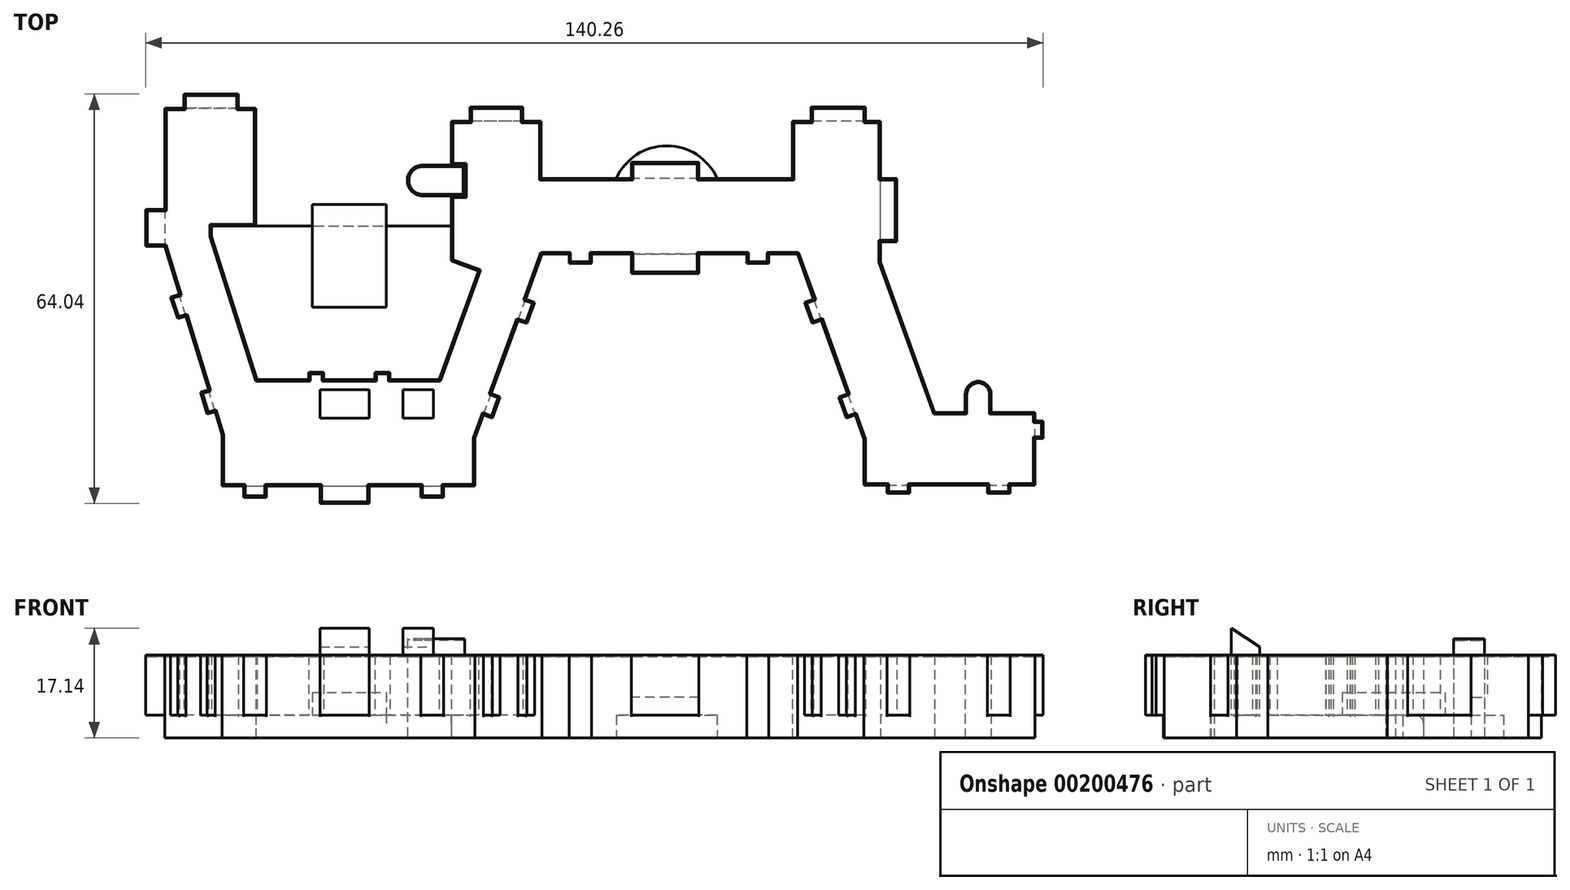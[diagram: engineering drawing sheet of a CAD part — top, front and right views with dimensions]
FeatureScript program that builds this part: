
annotation { "Feature Type Name" : "Feature", "Feature Type Description" : "" }
export const myFeature = defineFeature(function(context is Context, id is Id, definition is map)
    precondition{}
    {
        {
            var Q0;
            Q0=qCreatedBy(makeId("Top.planeOp"),FACE);
            var sketch = newSketch(context, id + "F0", { "sketchPlane" : qUnion([Q0])});
            skLineSegment(sketch, "E0", {"start": v(11.22, -2.24) * mm, "end": v(8.5, -2.24) * mm});
            skLineSegment(sketch, "E1", {"start": v(8.5, -2.24) * mm, "end": v(8.5, 0) * mm});
            skLineSegment(sketch, "E2", {"start": v(8.5, 0) * mm, "end": v(0, 0) * mm});
            skLineSegment(sketch, "E3", {"start": v(0, 0) * mm, "end": v(0, -2.24) * mm});
            skLineSegment(sketch, "E4", {"start": v(0, -2.24) * mm, "end": v(-3.01, -2.24) * mm});
            skLineSegment(sketch, "E5", {"start": v(-3.01, -2.24) * mm, "end": v(-3.01, -18.02) * mm});
            skLineSegment(sketch, "E6", {"start": v(-3.01, -18.02) * mm, "end": v(-6, -18.02) * mm});
            skLineSegment(sketch, "E7", {"start": v(-6, -18.02) * mm, "end": v(-6, -23.84) * mm});
            skLineSegment(sketch, "E8", {"start": v(-6, -23.84) * mm, "end": v(-3.01, -23.84) * mm});
            skLineSegment(sketch, "E9", {"start": v(-3.01, -23.84) * mm, "end": v(-0.72, -31.34) * mm});
            skLineSegment(sketch, "E10", {"start": v(-0.72, -31.34) * mm, "end": v(-2.13, -31.77) * mm});
            skLineSegment(sketch, "E11", {"start": v(-2.13, -31.77) * mm, "end": v(-0.97, -35.12) * mm});
            skLineSegment(sketch, "E12", {"start": v(-0.97, -35.12) * mm, "end": v(0.32, -34.73) * mm});
            skLineSegment(sketch, "E13", {"start": v(0.32, -34.73) * mm, "end": v(3.84, -46.26) * mm});
            skLineSegment(sketch, "E14", {"start": v(3.84, -46.26) * mm, "end": v(2.58, -46.65) * mm});
            skLineSegment(sketch, "E15", {"start": v(2.58, -46.65) * mm, "end": v(3.62, -50.04) * mm});
            skLineSegment(sketch, "E16", {"start": v(3.62, -50.04) * mm, "end": v(4.88, -49.65) * mm});
            skLineSegment(sketch, "E17", {"start": v(4.88, -49.65) * mm, "end": v(6, -53.3) * mm});
            skLineSegment(sketch, "E18", {"start": v(6, -53.3) * mm, "end": v(6, -61.28) * mm});
            skLineSegment(sketch, "E19", {"start": v(6, -61.28) * mm, "end": v(9.31, -61.28) * mm});
            skLineSegment(sketch, "E20", {"start": v(9.31, -61.28) * mm, "end": v(9.31, -63.05) * mm});
            skLineSegment(sketch, "E21", {"start": v(9.31, -63.05) * mm, "end": v(12.86, -63.05) * mm});
            skLineSegment(sketch, "E22", {"start": v(12.86, -63.05) * mm, "end": v(12.86, -61.28) * mm});
            skLineSegment(sketch, "E23", {"start": v(12.86, -61.28) * mm, "end": v(21.27, -61.28) * mm});
            skLineSegment(sketch, "E24", {"start": v(21.27, -61.28) * mm, "end": v(21.27, -64.04) * mm});
            skLineSegment(sketch, "E25", {"start": v(21.27, -64.04) * mm, "end": v(28.97, -64.04) * mm});
            skLineSegment(sketch, "E26", {"start": v(28.97, -64.04) * mm, "end": v(28.97, -61.28) * mm});
            skLineSegment(sketch, "E27", {"start": v(28.97, -61.28) * mm, "end": v(37, -61.28) * mm});
            skLineSegment(sketch, "E28", {"start": v(37, -61.28) * mm, "end": v(37, -63.05) * mm});
            skLineSegment(sketch, "E29", {"start": v(37, -63.05) * mm, "end": v(40.54, -63.05) * mm});
            skLineSegment(sketch, "E30", {"start": v(40.54, -63.05) * mm, "end": v(40.54, -61.28) * mm});
            skLineSegment(sketch, "E31", {"start": v(40.54, -61.28) * mm, "end": v(45.48, -61.28) * mm});
            skLineSegment(sketch, "E32", {"start": v(45.48, -61.28) * mm, "end": v(45.48, -53.82) * mm});
            skLineSegment(sketch, "E33", {"start": v(45.48, -53.82) * mm, "end": v(46.82, -50.15) * mm});
            skLineSegment(sketch, "E34", {"start": v(46.82, -50.15) * mm, "end": v(48.2, -50.7) * mm});
            skLineSegment(sketch, "E35", {"start": v(48.2, -50.7) * mm, "end": v(49.42, -47.37) * mm});
            skLineSegment(sketch, "E36", {"start": v(49.42, -47.37) * mm, "end": v(48.03, -46.82) * mm});
            skLineSegment(sketch, "E37", {"start": v(48.03, -46.82) * mm, "end": v(52.17, -35.43) * mm});
            skLineSegment(sketch, "E38", {"start": v(52.17, -35.43) * mm, "end": v(53.6, -35.9) * mm});
            skLineSegment(sketch, "E39", {"start": v(53.6, -35.9) * mm, "end": v(54.8, -32.57) * mm});
            skLineSegment(sketch, "E40", {"start": v(54.8, -32.57) * mm, "end": v(53.38, -32.1) * mm});
            skLineSegment(sketch, "E41", {"start": v(53.38, -32.1) * mm, "end": v(55.96, -25.02) * mm});
            skLineSegment(sketch, "E42", {"start": v(55.96, -25.02) * mm, "end": v(60.16, -25.02) * mm});
            skLineSegment(sketch, "E43", {"start": v(60.16, -25.02) * mm, "end": v(60.16, -26.52) * mm});
            skLineSegment(sketch, "E44", {"start": v(60.16, -26.52) * mm, "end": v(63.7, -26.52) * mm});
            skLineSegment(sketch, "E45", {"start": v(63.7, -26.52) * mm, "end": v(63.7, -25.02) * mm});
            skLineSegment(sketch, "E46", {"start": v(63.7, -25.02) * mm, "end": v(69.91, -25.02) * mm});
            skLineSegment(sketch, "E47", {"start": v(69.91, -25.02) * mm, "end": v(69.91, -28.1) * mm});
            skLineSegment(sketch, "E48", {"start": v(69.91, -28.1) * mm, "end": v(80.46, -28.1) * mm});
            skLineSegment(sketch, "E49", {"start": v(80.46, -28.1) * mm, "end": v(80.46, -25.02) * mm});
            skLineSegment(sketch, "E50", {"start": v(80.46, -25.02) * mm, "end": v(87.96, -25.02) * mm});
            skLineSegment(sketch, "E51", {"start": v(87.96, -25.02) * mm, "end": v(87.96, -26.52) * mm});
            skLineSegment(sketch, "E52", {"start": v(87.96, -26.52) * mm, "end": v(91.4, -26.52) * mm});
            skLineSegment(sketch, "E53", {"start": v(91.4, -26.52) * mm, "end": v(91.4, -25.02) * mm});
            skLineSegment(sketch, "E54", {"start": v(91.4, -25.02) * mm, "end": v(95.85, -25.02) * mm});
            skLineSegment(sketch, "E55", {"start": v(95.85, -25.02) * mm, "end": v(98.38, -32.06) * mm});
            skLineSegment(sketch, "E56", {"start": v(98.38, -32.06) * mm, "end": v(96.97, -32.57) * mm});
            skLineSegment(sketch, "E57", {"start": v(96.97, -32.57) * mm, "end": v(98.17, -35.9) * mm});
            skLineSegment(sketch, "E58", {"start": v(98.17, -35.9) * mm, "end": v(99.58, -35.4) * mm});
            skLineSegment(sketch, "E59", {"start": v(99.58, -35.4) * mm, "end": v(103.7, -46.87) * mm});
            skLineSegment(sketch, "E60", {"start": v(103.7, -46.87) * mm, "end": v(102.29, -47.37) * mm});
            skLineSegment(sketch, "E61", {"start": v(102.29, -47.37) * mm, "end": v(103.49, -50.7) * mm});
            skLineSegment(sketch, "E62", {"start": v(103.49, -50.7) * mm, "end": v(104.9, -50.2) * mm});
            skLineSegment(sketch, "E63", {"start": v(104.9, -50.2) * mm, "end": v(106.25, -53.96) * mm});
            skLineSegment(sketch, "E64", {"start": v(106.25, -53.96) * mm, "end": v(106.25, -61.16) * mm});
            skLineSegment(sketch, "E65", {"start": v(106.25, -61.16) * mm, "end": v(109.85, -61.16) * mm});
            skLineSegment(sketch, "E66", {"start": v(109.85, -61.16) * mm, "end": v(109.85, -62.43) * mm});
            skLineSegment(sketch, "E67", {"start": v(109.85, -62.43) * mm, "end": v(113.4, -62.43) * mm});
            skLineSegment(sketch, "E68", {"start": v(113.4, -62.43) * mm, "end": v(113.4, -61.16) * mm});
            skLineSegment(sketch, "E69", {"start": v(113.4, -61.16) * mm, "end": v(125.52, -61.16) * mm});
            skLineSegment(sketch, "E70", {"start": v(125.52, -61.16) * mm, "end": v(125.52, -62.43) * mm});
            skLineSegment(sketch, "E71", {"start": v(125.52, -62.43) * mm, "end": v(129.06, -62.43) * mm});
            skLineSegment(sketch, "E72", {"start": v(129.06, -62.43) * mm, "end": v(129.06, -61.16) * mm});
            skLineSegment(sketch, "E73", {"start": v(129.06, -61.16) * mm, "end": v(133, -61.16) * mm});
            skLineSegment(sketch, "E74", {"start": v(133, -61.16) * mm, "end": v(133, -53.89) * mm});
            skLineSegment(sketch, "E75", {"start": v(133, -53.89) * mm, "end": v(134.26, -53.89) * mm});
            skLineSegment(sketch, "E76", {"start": v(134.26, -53.89) * mm, "end": v(134.26, -51.15) * mm});
            skLineSegment(sketch, "E77", {"start": v(134.26, -51.15) * mm, "end": v(133, -51.15) * mm});
            skLineSegment(sketch, "E78", {"start": v(133, -51.15) * mm, "end": v(133, -49.82) * mm});
            skLineSegment(sketch, "E79", {"start": v(133, -49.82) * mm, "end": v(126.13, -49.82) * mm});
            skLineSegment(sketch, "E80", {"start": v(126.13, -49.82) * mm, "end": v(126.13, -46.96) * mm});
            skLineSegment(sketch, "E81", {"start": v(122.07, -46.96) * mm, "end": v(122.07, -49.82) * mm});
            skLineSegment(sketch, "E82", {"start": v(122.07, -49.82) * mm, "end": v(117.3, -49.82) * mm});
            skLineSegment(sketch, "E83", {"start": v(117.3, -49.82) * mm, "end": v(108.85, -26.28) * mm});
            skLineSegment(sketch, "E84", {"start": v(108.85, -26.28) * mm, "end": v(108.85, -23.13) * mm});
            skLineSegment(sketch, "E85", {"start": v(108.85, -23.13) * mm, "end": v(111.35, -23.13) * mm});
            skLineSegment(sketch, "E86", {"start": v(111.35, -23.13) * mm, "end": v(111.35, -13.22) * mm});
            skLineSegment(sketch, "E87", {"start": v(111.35, -13.22) * mm, "end": v(108.85, -13.22) * mm});
            skLineSegment(sketch, "E88", {"start": v(108.85, -13.22) * mm, "end": v(108.85, -4.25) * mm});
            skLineSegment(sketch, "E89", {"start": v(108.85, -4.25) * mm, "end": v(106.47, -4.25) * mm});
            skLineSegment(sketch, "E90", {"start": v(106.47, -4.25) * mm, "end": v(106.47, -2.03) * mm});
            skLineSegment(sketch, "E91", {"start": v(106.47, -2.03) * mm, "end": v(98, -2.03) * mm});
            skLineSegment(sketch, "E92", {"start": v(98, -2.03) * mm, "end": v(98, -4.25) * mm});
            skLineSegment(sketch, "E93", {"start": v(98, -4.25) * mm, "end": v(95.07, -4.25) * mm});
            skLineSegment(sketch, "E94", {"start": v(95.07, -4.25) * mm, "end": v(95.07, -13.22) * mm});
            skLineSegment(sketch, "E95", {"start": v(95.07, -13.22) * mm, "end": v(80.46, -13.22) * mm});
            skLineSegment(sketch, "E96", {"start": v(80.46, -13.22) * mm, "end": v(80.46, -10.66) * mm});
            skLineSegment(sketch, "E97", {"start": v(80.46, -10.66) * mm, "end": v(69.91, -10.66) * mm});
            skLineSegment(sketch, "E98", {"start": v(69.91, -10.66) * mm, "end": v(69.91, -13.22) * mm});
            skLineSegment(sketch, "E99", {"start": v(69.91, -13.22) * mm, "end": v(55.8, -13.22) * mm});
            skLineSegment(sketch, "E100", {"start": v(55.8, -13.22) * mm, "end": v(55.8, -4.25) * mm});
            skLineSegment(sketch, "E101", {"start": v(55.8, -4.25) * mm, "end": v(52.93, -4.25) * mm});
            skLineSegment(sketch, "E102", {"start": v(52.93, -4.25) * mm, "end": v(52.93, -2.03) * mm});
            skLineSegment(sketch, "E103", {"start": v(52.93, -2.03) * mm, "end": v(44.68, -2.03) * mm});
            skLineSegment(sketch, "E104", {"start": v(44.68, -2.03) * mm, "end": v(44.68, -4.25) * mm});
            skLineSegment(sketch, "E105", {"start": v(44.68, -4.25) * mm, "end": v(41.8, -4.25) * mm});
            skLineSegment(sketch, "E106", {"start": v(41.8, -4.25) * mm, "end": v(41.8, -11.12) * mm});
            skLineSegment(sketch, "E107", {"start": v(41.8, -11.12) * mm, "end": v(37.3, -11.12) * mm});
            skLineSegment(sketch, "E108", {"start": v(37.3, -15.94) * mm, "end": v(41.79, -15.94) * mm});
            skLineSegment(sketch, "E109", {"start": v(41.79, -15.94) * mm, "end": v(41.79, -26.13) * mm});
            skLineSegment(sketch, "E110", {"start": v(41.79, -26.13) * mm, "end": v(46.05, -27.68) * mm});
            skLineSegment(sketch, "E111", {"start": v(46.05, -27.68) * mm, "end": v(39.88, -44.65) * mm});
            skLineSegment(sketch, "E112", {"start": v(39.88, -44.65) * mm, "end": v(32.18, -44.65) * mm});
            skLineSegment(sketch, "E113", {"start": v(32.18, -44.65) * mm, "end": v(32.18, -43.48) * mm});
            skLineSegment(sketch, "E114", {"start": v(32.18, -43.48) * mm, "end": v(29.86, -43.48) * mm});
            skLineSegment(sketch, "E115", {"start": v(29.86, -43.48) * mm, "end": v(29.86, -44.65) * mm});
            skLineSegment(sketch, "E116", {"start": v(29.86, -44.65) * mm, "end": v(21.83, -44.65) * mm});
            skLineSegment(sketch, "E117", {"start": v(21.83, -44.65) * mm, "end": v(21.83, -43.48) * mm});
            skLineSegment(sketch, "E118", {"start": v(21.83, -43.48) * mm, "end": v(19.5, -43.48) * mm});
            skLineSegment(sketch, "E119", {"start": v(19.5, -43.48) * mm, "end": v(19.5, -44.65) * mm});
            skLineSegment(sketch, "E120", {"start": v(19.5, -44.65) * mm, "end": v(11.42, -44.65) * mm});
            skLineSegment(sketch, "E121", {"start": v(11.42, -44.65) * mm, "end": v(4.3, -22.29) * mm});
            skLineSegment(sketch, "E122", {"start": v(4.3, -22.29) * mm, "end": v(4.3, -20.63) * mm});
            skLineSegment(sketch, "E123", {"start": v(4.3, -20.63) * mm, "end": v(11.22, -20.63) * mm});
            skLineSegment(sketch, "E124", {"start": v(11.22, -20.63) * mm, "end": v(11.22, -2.24) * mm});
            skArc(sketch, "E125", {"start": v(37.3, -11.12) * mm, "mid": v(34.9, -13.53) * mm, "end": v(37.3, -15.94) * mm});
            skArc(sketch, "E126", {"start": v(126.13, -46.96) * mm, "mid": v(124.1, -44.93) * mm, "end": v(122.07, -46.96) * mm});
            skLineSegment(sketch, "E127", {"start": v(41.8, -11.12) * mm, "end": v(43.9, -11.12) * mm});
            skLineSegment(sketch, "E128", {"start": v(43.9, -11.12) * mm, "end": v(43.9, -15.94) * mm});
            skLineSegment(sketch, "E129", {"start": v(43.9, -15.94) * mm, "end": v(41.79, -15.94) * mm});
            skLineSegment(sketch, "E130", {"start": v(-3.01, -18.02) * mm, "end": v(-3.01, -23.84) * mm, "construction": true});
            skSolve(sketch);
        }
        {
            var Q0;
            Q0 = qSketchRegion(id + "F0", true);
            extrude(context, id + "F1", {"entities" : qUnion([Q0]), "depth" : 12.7 * mm});
        }
        {
            var Q0;
            Q0=makeQuery(id+"F0.imprint","IMPRINT",FACE,{"disambiguationData":[TD([[makeQuery(id+"F0.imprint","IMPRINT",EDGE,{"derivedFrom":sQuery(id+"F0.wireOp",EDGE,"E107")}),1.0]])]});
            extrude(context, id + "F2", {"entities" : qUnion([Q0]), "operationType" : NewBodyOperationType.ADD, "depth" : 15.24 * mm});
        }
        {
            var Q0;
            Q0=makeQuery(id+"F1.opExtrude","CAP_FACE",FACE,{"disambiguationData":[OSD([sQuery(id+"F0.wireOp",EDGE,"E0"),sQuery(id+"F0.wireOp",EDGE,"E1"),sQuery(id+"F0.wireOp",EDGE,"E2"),sQuery(id+"F0.wireOp",EDGE,"E3"),sQuery(id+"F0.wireOp",EDGE,"E4"),sQuery(id+"F0.wireOp",EDGE,"E5"),sQuery(id+"F0.wireOp",EDGE,"E6"),sQuery(id+"F0.wireOp",EDGE,"E7"),sQuery(id+"F0.wireOp",EDGE,"E8"),sQuery(id+"F0.wireOp",EDGE,"E9"),sQuery(id+"F0.wireOp",EDGE,"E10"),sQuery(id+"F0.wireOp",EDGE,"E11"),sQuery(id+"F0.wireOp",EDGE,"E12"),sQuery(id+"F0.wireOp",EDGE,"E13"),sQuery(id+"F0.wireOp",EDGE,"E14"),sQuery(id+"F0.wireOp",EDGE,"E15"),sQuery(id+"F0.wireOp",EDGE,"E16"),sQuery(id+"F0.wireOp",EDGE,"E17"),sQuery(id+"F0.wireOp",EDGE,"E18"),sQuery(id+"F0.wireOp",EDGE,"E19"),sQuery(id+"F0.wireOp",EDGE,"E20"),sQuery(id+"F0.wireOp",EDGE,"E21"),sQuery(id+"F0.wireOp",EDGE,"E22"),sQuery(id+"F0.wireOp",EDGE,"E23"),sQuery(id+"F0.wireOp",EDGE,"E24"),sQuery(id+"F0.wireOp",EDGE,"E25"),sQuery(id+"F0.wireOp",EDGE,"E26"),sQuery(id+"F0.wireOp",EDGE,"E27"),sQuery(id+"F0.wireOp",EDGE,"E28"),sQuery(id+"F0.wireOp",EDGE,"E29"),sQuery(id+"F0.wireOp",EDGE,"E30"),sQuery(id+"F0.wireOp",EDGE,"E31"),sQuery(id+"F0.wireOp",EDGE,"E32"),sQuery(id+"F0.wireOp",EDGE,"E33"),sQuery(id+"F0.wireOp",EDGE,"E34"),sQuery(id+"F0.wireOp",EDGE,"E35"),sQuery(id+"F0.wireOp",EDGE,"E36"),sQuery(id+"F0.wireOp",EDGE,"E37"),sQuery(id+"F0.wireOp",EDGE,"E38"),sQuery(id+"F0.wireOp",EDGE,"E39"),sQuery(id+"F0.wireOp",EDGE,"E40"),sQuery(id+"F0.wireOp",EDGE,"E41"),sQuery(id+"F0.wireOp",EDGE,"E42"),sQuery(id+"F0.wireOp",EDGE,"E43"),sQuery(id+"F0.wireOp",EDGE,"E44"),sQuery(id+"F0.wireOp",EDGE,"E45"),sQuery(id+"F0.wireOp",EDGE,"E46"),sQuery(id+"F0.wireOp",EDGE,"E47"),sQuery(id+"F0.wireOp",EDGE,"E48"),sQuery(id+"F0.wireOp",EDGE,"E49"),sQuery(id+"F0.wireOp",EDGE,"E50"),sQuery(id+"F0.wireOp",EDGE,"E51"),sQuery(id+"F0.wireOp",EDGE,"E52"),sQuery(id+"F0.wireOp",EDGE,"E53"),sQuery(id+"F0.wireOp",EDGE,"E54"),sQuery(id+"F0.wireOp",EDGE,"E55"),sQuery(id+"F0.wireOp",EDGE,"E56"),sQuery(id+"F0.wireOp",EDGE,"E57"),sQuery(id+"F0.wireOp",EDGE,"E58"),sQuery(id+"F0.wireOp",EDGE,"E59"),sQuery(id+"F0.wireOp",EDGE,"E60"),sQuery(id+"F0.wireOp",EDGE,"E61"),sQuery(id+"F0.wireOp",EDGE,"E62"),sQuery(id+"F0.wireOp",EDGE,"E63"),sQuery(id+"F0.wireOp",EDGE,"E64"),sQuery(id+"F0.wireOp",EDGE,"E65"),sQuery(id+"F0.wireOp",EDGE,"E66"),sQuery(id+"F0.wireOp",EDGE,"E67"),sQuery(id+"F0.wireOp",EDGE,"E68"),sQuery(id+"F0.wireOp",EDGE,"E69"),sQuery(id+"F0.wireOp",EDGE,"E70"),sQuery(id+"F0.wireOp",EDGE,"E71"),sQuery(id+"F0.wireOp",EDGE,"E72"),sQuery(id+"F0.wireOp",EDGE,"E73"),sQuery(id+"F0.wireOp",EDGE,"E74"),sQuery(id+"F0.wireOp",EDGE,"E75"),sQuery(id+"F0.wireOp",EDGE,"E76"),sQuery(id+"F0.wireOp",EDGE,"E77"),sQuery(id+"F0.wireOp",EDGE,"E78"),sQuery(id+"F0.wireOp",EDGE,"E79"),sQuery(id+"F0.wireOp",EDGE,"E80"),sQuery(id+"F0.wireOp",EDGE,"E81"),sQuery(id+"F0.wireOp",EDGE,"E82"),sQuery(id+"F0.wireOp",EDGE,"E83"),sQuery(id+"F0.wireOp",EDGE,"E84"),sQuery(id+"F0.wireOp",EDGE,"E85"),sQuery(id+"F0.wireOp",EDGE,"E86"),sQuery(id+"F0.wireOp",EDGE,"E87"),sQuery(id+"F0.wireOp",EDGE,"E88"),sQuery(id+"F0.wireOp",EDGE,"E89"),sQuery(id+"F0.wireOp",EDGE,"E90"),sQuery(id+"F0.wireOp",EDGE,"E91"),sQuery(id+"F0.wireOp",EDGE,"E92"),sQuery(id+"F0.wireOp",EDGE,"E93"),sQuery(id+"F0.wireOp",EDGE,"E94"),sQuery(id+"F0.wireOp",EDGE,"E95"),sQuery(id+"F0.wireOp",EDGE,"E96"),sQuery(id+"F0.wireOp",EDGE,"E97"),sQuery(id+"F0.wireOp",EDGE,"E98"),sQuery(id+"F0.wireOp",EDGE,"E99"),sQuery(id+"F0.wireOp",EDGE,"E100"),sQuery(id+"F0.wireOp",EDGE,"E101"),sQuery(id+"F0.wireOp",EDGE,"E102"),sQuery(id+"F0.wireOp",EDGE,"E103"),sQuery(id+"F0.wireOp",EDGE,"E104"),sQuery(id+"F0.wireOp",EDGE,"E105"),sQuery(id+"F0.wireOp",EDGE,"E106"),sQuery(id+"F0.wireOp",EDGE,"E107"),sQuery(id+"F0.wireOp",EDGE,"E108"),sQuery(id+"F0.wireOp",EDGE,"E109"),sQuery(id+"F0.wireOp",EDGE,"E110"),sQuery(id+"F0.wireOp",EDGE,"E111"),sQuery(id+"F0.wireOp",EDGE,"E112"),sQuery(id+"F0.wireOp",EDGE,"E113"),sQuery(id+"F0.wireOp",EDGE,"E114"),sQuery(id+"F0.wireOp",EDGE,"E115"),sQuery(id+"F0.wireOp",EDGE,"E116"),sQuery(id+"F0.wireOp",EDGE,"E117"),sQuery(id+"F0.wireOp",EDGE,"E118"),sQuery(id+"F0.wireOp",EDGE,"E119"),sQuery(id+"F0.wireOp",EDGE,"E120"),sQuery(id+"F0.wireOp",EDGE,"E121"),sQuery(id+"F0.wireOp",EDGE,"E122"),sQuery(id+"F0.wireOp",EDGE,"E123"),sQuery(id+"F0.wireOp",EDGE,"E124"),sQuery(id+"F0.wireOp",EDGE,"E125"),sQuery(id+"F0.wireOp",EDGE,"E126")])],"isStart":false});
            var sketch = newSketch(context, id + "F3", { "sketchPlane" : qUnion([Q0])});
            skLineSegment(sketch, "E131.0", {"start": v(42.05, -4.5) * mm, "end": v(42.05, -10.87) * mm});
            skLineSegment(sketch, "E131.1", {"start": v(44.93, -4.5) * mm, "end": v(42.05, -4.5) * mm});
            skLineSegment(sketch, "E131.2", {"start": v(44.93, -2.28) * mm, "end": v(44.93, -4.5) * mm});
            skLineSegment(sketch, "E131.3", {"start": v(52.68, -2.28) * mm, "end": v(44.93, -2.28) * mm});
            skLineSegment(sketch, "E131.4", {"start": v(52.68, -4.5) * mm, "end": v(52.68, -2.28) * mm});
            skLineSegment(sketch, "E131.5", {"start": v(55.56, -4.5) * mm, "end": v(52.68, -4.5) * mm});
            skLineSegment(sketch, "E131.6", {"start": v(55.56, -13.47) * mm, "end": v(55.56, -4.5) * mm});
            skLineSegment(sketch, "E131.7", {"start": v(70.17, -13.47) * mm, "end": v(55.56, -13.47) * mm});
            skLineSegment(sketch, "E131.8", {"start": v(70.17, -10.91) * mm, "end": v(70.17, -13.47) * mm});
            skLineSegment(sketch, "E131.9", {"start": v(80.2, -10.91) * mm, "end": v(70.17, -10.91) * mm});
            skLineSegment(sketch, "E131.10", {"start": v(80.2, -13.47) * mm, "end": v(80.2, -10.91) * mm});
            skLineSegment(sketch, "E131.11", {"start": v(95.32, -13.47) * mm, "end": v(80.2, -13.47) * mm});
            skLineSegment(sketch, "E131.12", {"start": v(95.32, -4.5) * mm, "end": v(95.32, -13.47) * mm});
            skLineSegment(sketch, "E131.13", {"start": v(98.26, -4.5) * mm, "end": v(95.32, -4.5) * mm});
            skLineSegment(sketch, "E131.14", {"start": v(98.26, -2.28) * mm, "end": v(98.26, -4.5) * mm});
            skLineSegment(sketch, "E131.15", {"start": v(106.22, -2.28) * mm, "end": v(98.26, -2.28) * mm});
            skLineSegment(sketch, "E131.16", {"start": v(106.22, -4.5) * mm, "end": v(106.22, -2.28) * mm});
            skLineSegment(sketch, "E131.17", {"start": v(108.6, -4.5) * mm, "end": v(106.22, -4.5) * mm});
            skLineSegment(sketch, "E131.18", {"start": v(108.6, -13.47) * mm, "end": v(108.6, -4.5) * mm});
            skLineSegment(sketch, "E131.19", {"start": v(111.1, -13.47) * mm, "end": v(108.6, -13.47) * mm});
            skLineSegment(sketch, "E131.20", {"start": v(111.1, -22.87) * mm, "end": v(111.1, -13.47) * mm});
            skLineSegment(sketch, "E131.21", {"start": v(108.6, -22.87) * mm, "end": v(111.1, -22.87) * mm});
            skLineSegment(sketch, "E131.22", {"start": v(108.6, -26.33) * mm, "end": v(108.6, -22.87) * mm});
            skLineSegment(sketch, "E131.23", {"start": v(117.13, -50.07) * mm, "end": v(108.6, -26.33) * mm});
            skLineSegment(sketch, "E131.24", {"start": v(122.32, -50.07) * mm, "end": v(117.13, -50.07) * mm});
            skLineSegment(sketch, "E131.25", {"start": v(122.32, -46.96) * mm, "end": v(122.32, -50.07) * mm});
            skArc(sketch, "E131.26", {"start": v(125.87, -46.96) * mm, "mid": v(124.1, -45.19) * mm, "end": v(122.32, -46.96) * mm});
            skLineSegment(sketch, "E131.27", {"start": v(125.87, -50.07) * mm, "end": v(125.87, -46.96) * mm});
            skLineSegment(sketch, "E131.28", {"start": v(132.74, -50.07) * mm, "end": v(125.87, -50.07) * mm});
            skLineSegment(sketch, "E131.29", {"start": v(132.74, -51.4) * mm, "end": v(132.74, -50.07) * mm});
            skLineSegment(sketch, "E131.30", {"start": v(28.72, -61.02) * mm, "end": v(37.25, -61.02) * mm});
            skLineSegment(sketch, "E131.31", {"start": v(28.72, -63.8) * mm, "end": v(28.72, -61.02) * mm});
            skLineSegment(sketch, "E131.32", {"start": v(21.53, -63.8) * mm, "end": v(28.72, -63.8) * mm});
            skLineSegment(sketch, "E131.33", {"start": v(21.53, -61.02) * mm, "end": v(21.53, -63.8) * mm});
            skLineSegment(sketch, "E131.34", {"start": v(12.6, -61.02) * mm, "end": v(21.53, -61.02) * mm});
            skLineSegment(sketch, "E131.35", {"start": v(12.6, -62.8) * mm, "end": v(12.6, -61.02) * mm});
            skLineSegment(sketch, "E131.36", {"start": v(9.57, -62.8) * mm, "end": v(12.6, -62.8) * mm});
            skLineSegment(sketch, "E131.37", {"start": v(9.57, -61.02) * mm, "end": v(9.57, -62.8) * mm});
            skLineSegment(sketch, "E131.38", {"start": v(6.25, -61.02) * mm, "end": v(9.57, -61.02) * mm});
            skLineSegment(sketch, "E131.39", {"start": v(6.25, -53.27) * mm, "end": v(6.25, -61.02) * mm});
            skLineSegment(sketch, "E131.40", {"start": v(5.04, -49.34) * mm, "end": v(6.25, -53.27) * mm});
            skLineSegment(sketch, "E131.41", {"start": v(3.79, -49.72) * mm, "end": v(5.04, -49.34) * mm});
            skLineSegment(sketch, "E131.42", {"start": v(2.9, -46.82) * mm, "end": v(3.79, -49.72) * mm});
            skLineSegment(sketch, "E131.43", {"start": v(4.16, -46.43) * mm, "end": v(2.9, -46.82) * mm});
            skLineSegment(sketch, "E131.44", {"start": v(0.48, -34.4) * mm, "end": v(4.16, -46.43) * mm});
            skLineSegment(sketch, "E131.45", {"start": v(-0.81, -34.8) * mm, "end": v(0.48, -34.4) * mm});
            skLineSegment(sketch, "E131.46", {"start": v(-1.8, -31.94) * mm, "end": v(-0.81, -34.8) * mm});
            skLineSegment(sketch, "E131.47", {"start": v(-0.4, -31.5) * mm, "end": v(-1.8, -31.94) * mm});
            skLineSegment(sketch, "E131.48", {"start": v(-2.82, -23.58) * mm, "end": v(-0.4, -31.5) * mm});
            skLineSegment(sketch, "E131.49", {"start": v(-5.75, -23.58) * mm, "end": v(-2.82, -23.58) * mm});
            skLineSegment(sketch, "E131.50", {"start": v(-5.75, -18.28) * mm, "end": v(-5.75, -23.58) * mm});
            skLineSegment(sketch, "E131.51", {"start": v(-2.76, -18.28) * mm, "end": v(-5.75, -18.28) * mm});
            skLineSegment(sketch, "E131.52", {"start": v(-2.76, -2.5) * mm, "end": v(-2.76, -18.28) * mm});
            skLineSegment(sketch, "E131.53", {"start": v(0.25, -2.5) * mm, "end": v(-2.76, -2.5) * mm});
            skLineSegment(sketch, "E131.54", {"start": v(30.1, -44.9) * mm, "end": v(21.57, -44.9) * mm});
            skLineSegment(sketch, "E131.55", {"start": v(30.1, -43.74) * mm, "end": v(30.1, -44.9) * mm});
            skLineSegment(sketch, "E131.56", {"start": v(31.93, -43.74) * mm, "end": v(30.1, -43.74) * mm});
            skLineSegment(sketch, "E131.57", {"start": v(31.93, -44.9) * mm, "end": v(31.93, -43.74) * mm});
            skLineSegment(sketch, "E131.58", {"start": v(40.06, -44.9) * mm, "end": v(31.93, -44.9) * mm});
            skLineSegment(sketch, "E131.59", {"start": v(46.37, -27.52) * mm, "end": v(40.06, -44.9) * mm});
            skLineSegment(sketch, "E131.60", {"start": v(44.16, -10.87) * mm, "end": v(44.16, -16.2) * mm});
            skLineSegment(sketch, "E131.61", {"start": v(44.16, -16.2) * mm, "end": v(42.04, -16.2) * mm});
            skLineSegment(sketch, "E131.62", {"start": v(42.04, -16.2) * mm, "end": v(42.04, -25.95) * mm});
            skLineSegment(sketch, "E131.63", {"start": v(42.04, -25.95) * mm, "end": v(46.37, -27.52) * mm});
            skLineSegment(sketch, "E131.64", {"start": v(21.57, -44.9) * mm, "end": v(21.57, -43.74) * mm});
            skLineSegment(sketch, "E131.65", {"start": v(21.57, -43.74) * mm, "end": v(19.76, -43.74) * mm});
            skLineSegment(sketch, "E131.66", {"start": v(19.76, -43.74) * mm, "end": v(19.76, -44.9) * mm});
            skLineSegment(sketch, "E131.67", {"start": v(19.76, -44.9) * mm, "end": v(11.23, -44.9) * mm});
            skLineSegment(sketch, "E131.68", {"start": v(11.23, -44.9) * mm, "end": v(4.04, -22.33) * mm});
            skLineSegment(sketch, "E131.69", {"start": v(4.04, -22.33) * mm, "end": v(4.04, -20.37) * mm});
            skLineSegment(sketch, "E131.70", {"start": v(4.04, -20.37) * mm, "end": v(10.96, -20.37) * mm});
            skLineSegment(sketch, "E131.71", {"start": v(10.96, -20.37) * mm, "end": v(10.96, -2.5) * mm});
            skLineSegment(sketch, "E131.72", {"start": v(10.96, -2.5) * mm, "end": v(8.25, -2.5) * mm});
            skLineSegment(sketch, "E131.73", {"start": v(8.25, -2.5) * mm, "end": v(8.25, -0.25) * mm});
            skLineSegment(sketch, "E131.74", {"start": v(8.25, -0.25) * mm, "end": v(0.25, -0.25) * mm});
            skLineSegment(sketch, "E131.75", {"start": v(0.25, -0.25) * mm, "end": v(0.25, -2.5) * mm});
            skLineSegment(sketch, "E131.76", {"start": v(37.25, -61.02) * mm, "end": v(37.25, -62.8) * mm});
            skLineSegment(sketch, "E131.77", {"start": v(37.25, -62.8) * mm, "end": v(40.29, -62.8) * mm});
            skLineSegment(sketch, "E131.78", {"start": v(40.29, -62.8) * mm, "end": v(40.29, -61.02) * mm});
            skLineSegment(sketch, "E131.79", {"start": v(40.29, -61.02) * mm, "end": v(45.23, -61.02) * mm});
            skLineSegment(sketch, "E131.80", {"start": v(45.23, -61.02) * mm, "end": v(45.23, -53.78) * mm});
            skLineSegment(sketch, "E131.81", {"start": v(45.23, -53.78) * mm, "end": v(46.67, -49.82) * mm});
            skLineSegment(sketch, "E131.82", {"start": v(46.67, -49.82) * mm, "end": v(48.06, -50.37) * mm});
            skLineSegment(sketch, "E131.83", {"start": v(48.06, -50.37) * mm, "end": v(49.1, -47.52) * mm});
            skLineSegment(sketch, "E131.84", {"start": v(49.1, -47.52) * mm, "end": v(47.7, -46.97) * mm});
            skLineSegment(sketch, "E131.85", {"start": v(47.7, -46.97) * mm, "end": v(52.02, -35.1) * mm});
            skLineSegment(sketch, "E131.86", {"start": v(52.02, -35.1) * mm, "end": v(53.44, -35.58) * mm});
            skLineSegment(sketch, "E131.87", {"start": v(53.44, -35.58) * mm, "end": v(54.48, -32.73) * mm});
            skLineSegment(sketch, "E131.88", {"start": v(54.48, -32.73) * mm, "end": v(53.05, -32.26) * mm});
            skLineSegment(sketch, "E131.89", {"start": v(53.05, -32.26) * mm, "end": v(55.78, -24.77) * mm});
            skLineSegment(sketch, "E131.90", {"start": v(55.78, -24.77) * mm, "end": v(60.42, -24.77) * mm});
            skLineSegment(sketch, "E131.91", {"start": v(60.42, -24.77) * mm, "end": v(60.42, -26.27) * mm});
            skLineSegment(sketch, "E131.92", {"start": v(60.42, -26.27) * mm, "end": v(63.45, -26.27) * mm});
            skLineSegment(sketch, "E131.93", {"start": v(63.45, -26.27) * mm, "end": v(63.45, -24.77) * mm});
            skLineSegment(sketch, "E131.94", {"start": v(63.45, -24.77) * mm, "end": v(70.17, -24.77) * mm});
            skLineSegment(sketch, "E131.95", {"start": v(70.17, -24.77) * mm, "end": v(70.17, -27.85) * mm});
            skLineSegment(sketch, "E131.96", {"start": v(70.17, -27.85) * mm, "end": v(80.2, -27.85) * mm});
            skLineSegment(sketch, "E131.97", {"start": v(80.2, -27.85) * mm, "end": v(80.2, -24.77) * mm});
            skLineSegment(sketch, "E131.98", {"start": v(80.2, -24.77) * mm, "end": v(88.21, -24.77) * mm});
            skLineSegment(sketch, "E131.99", {"start": v(88.21, -24.77) * mm, "end": v(88.21, -26.27) * mm});
            skLineSegment(sketch, "E131.100", {"start": v(88.21, -26.27) * mm, "end": v(91.14, -26.27) * mm});
            skLineSegment(sketch, "E131.101", {"start": v(91.14, -26.27) * mm, "end": v(91.14, -24.77) * mm});
            skLineSegment(sketch, "E131.102", {"start": v(91.14, -24.77) * mm, "end": v(96.03, -24.77) * mm});
            skLineSegment(sketch, "E131.103", {"start": v(96.03, -24.77) * mm, "end": v(98.7, -32.22) * mm});
            skLineSegment(sketch, "E131.104", {"start": v(98.7, -32.22) * mm, "end": v(97.3, -32.72) * mm});
            skLineSegment(sketch, "E131.105", {"start": v(97.3, -32.72) * mm, "end": v(98.32, -35.58) * mm});
            skLineSegment(sketch, "E131.106", {"start": v(42.05, -10.87) * mm, "end": v(44.16, -10.87) * mm});
            skLineSegment(sketch, "E131.107", {"start": v(98.32, -35.58) * mm, "end": v(99.73, -35.07) * mm});
            skLineSegment(sketch, "E131.108", {"start": v(99.73, -35.07) * mm, "end": v(104.02, -47.02) * mm});
            skLineSegment(sketch, "E131.109", {"start": v(104.02, -47.02) * mm, "end": v(102.61, -47.53) * mm});
            skLineSegment(sketch, "E131.110", {"start": v(102.61, -47.53) * mm, "end": v(103.64, -50.38) * mm});
            skLineSegment(sketch, "E131.111", {"start": v(103.64, -50.38) * mm, "end": v(105.05, -49.88) * mm});
            skLineSegment(sketch, "E131.112", {"start": v(105.05, -49.88) * mm, "end": v(106.5, -53.92) * mm});
            skLineSegment(sketch, "E131.113", {"start": v(106.5, -53.92) * mm, "end": v(106.5, -60.9) * mm});
            skLineSegment(sketch, "E131.114", {"start": v(106.5, -60.9) * mm, "end": v(110.1, -60.9) * mm});
            skLineSegment(sketch, "E131.115", {"start": v(110.1, -60.9) * mm, "end": v(110.1, -62.18) * mm});
            skLineSegment(sketch, "E131.116", {"start": v(110.1, -62.18) * mm, "end": v(113.14, -62.18) * mm});
            skLineSegment(sketch, "E131.117", {"start": v(113.14, -62.18) * mm, "end": v(113.14, -60.9) * mm});
            skLineSegment(sketch, "E131.118", {"start": v(113.14, -60.9) * mm, "end": v(125.77, -60.9) * mm});
            skLineSegment(sketch, "E131.119", {"start": v(125.77, -60.9) * mm, "end": v(125.77, -62.18) * mm});
            skLineSegment(sketch, "E131.120", {"start": v(125.77, -62.18) * mm, "end": v(128.8, -62.18) * mm});
            skLineSegment(sketch, "E131.121", {"start": v(128.8, -62.18) * mm, "end": v(128.8, -60.9) * mm});
            skLineSegment(sketch, "E131.122", {"start": v(128.8, -60.9) * mm, "end": v(132.74, -60.9) * mm});
            skLineSegment(sketch, "E131.123", {"start": v(132.74, -60.9) * mm, "end": v(132.74, -53.63) * mm});
            skLineSegment(sketch, "E131.124", {"start": v(132.74, -53.63) * mm, "end": v(134.01, -53.63) * mm});
            skLineSegment(sketch, "E131.125", {"start": v(134.01, -53.63) * mm, "end": v(134.01, -51.4) * mm});
            skLineSegment(sketch, "E131.126", {"start": v(134.01, -51.4) * mm, "end": v(132.74, -51.4) * mm});
            skSolve(sketch);
        }
        {
            var Q0;
            Q0=makeQuery(id+"F3.imprint","IMPRINT",FACE,{"disambiguationData":[TD([[makeQuery(id+"F3.imprint","IMPRINT",EDGE,{"derivedFrom":sQuery(id+"F3.wireOp",EDGE,"E131.0")}),-1.0]])]});
            extrude(context, id + "F4", {"entities" : qUnion([Q0]), "operationType" : NewBodyOperationType.ADD, "depth" : 0.25 * mm});
        }
        {
            var Q0;
            Q0=makeQuery(id+"F2.opExtrude","CAP_FACE",FACE,{"disambiguationData":[OSD([sQuery(id+"F0.wireOp",EDGE,"E107"),sQuery(id+"F0.wireOp",EDGE,"E108"),sQuery(id+"F0.wireOp",EDGE,"E125"),sQuery(id+"F0.wireOp",EDGE,"E127"),sQuery(id+"F0.wireOp",EDGE,"E128"),sQuery(id+"F0.wireOp",EDGE,"E129")])],"isStart":false});
            var sketch = newSketch(context, id + "F5", { "sketchPlane" : qUnion([Q0])});
            skLineSegment(sketch, "E132.0", {"start": v(43.65, -11.37) * mm, "end": v(37.3, -11.37) * mm});
            skLineSegment(sketch, "E132.1", {"start": v(43.65, -15.68) * mm, "end": v(43.65, -11.37) * mm});
            skLineSegment(sketch, "E132.2", {"start": v(37.3, -15.68) * mm, "end": v(43.65, -15.68) * mm});
            skArc(sketch, "E132.3", {"start": v(37.3, -11.37) * mm, "mid": v(35.15, -13.53) * mm, "end": v(37.3, -15.68) * mm});
            skSolve(sketch);
        }
        {
            var Q0;
            Q0=makeQuery(id+"F5.imprint","IMPRINT",FACE,{"disambiguationData":[TD([[makeQuery(id+"F5.imprint","IMPRINT",EDGE,{"derivedFrom":sQuery(id+"F5.wireOp",EDGE,"E132.0")}),-1.0]])]});
            extrude(context, id + "F6", {"entities" : qUnion([Q0]), "operationType" : NewBodyOperationType.ADD, "depth" : 0.25 * mm});
        }
        {
            var Q0;
            Q0=makeQuery(id+"F1.opExtrude","CAP_FACE",FACE,{"disambiguationData":[OSD([sQuery(id+"F0.wireOp",EDGE,"E0"),sQuery(id+"F0.wireOp",EDGE,"E1"),sQuery(id+"F0.wireOp",EDGE,"E2"),sQuery(id+"F0.wireOp",EDGE,"E3"),sQuery(id+"F0.wireOp",EDGE,"E4"),sQuery(id+"F0.wireOp",EDGE,"E5"),sQuery(id+"F0.wireOp",EDGE,"E6"),sQuery(id+"F0.wireOp",EDGE,"E7"),sQuery(id+"F0.wireOp",EDGE,"E8"),sQuery(id+"F0.wireOp",EDGE,"E9"),sQuery(id+"F0.wireOp",EDGE,"E10"),sQuery(id+"F0.wireOp",EDGE,"E11"),sQuery(id+"F0.wireOp",EDGE,"E12"),sQuery(id+"F0.wireOp",EDGE,"E13"),sQuery(id+"F0.wireOp",EDGE,"E14"),sQuery(id+"F0.wireOp",EDGE,"E15"),sQuery(id+"F0.wireOp",EDGE,"E16"),sQuery(id+"F0.wireOp",EDGE,"E17"),sQuery(id+"F0.wireOp",EDGE,"E18"),sQuery(id+"F0.wireOp",EDGE,"E19"),sQuery(id+"F0.wireOp",EDGE,"E20"),sQuery(id+"F0.wireOp",EDGE,"E21"),sQuery(id+"F0.wireOp",EDGE,"E22"),sQuery(id+"F0.wireOp",EDGE,"E23"),sQuery(id+"F0.wireOp",EDGE,"E24"),sQuery(id+"F0.wireOp",EDGE,"E25"),sQuery(id+"F0.wireOp",EDGE,"E26"),sQuery(id+"F0.wireOp",EDGE,"E27"),sQuery(id+"F0.wireOp",EDGE,"E28"),sQuery(id+"F0.wireOp",EDGE,"E29"),sQuery(id+"F0.wireOp",EDGE,"E30"),sQuery(id+"F0.wireOp",EDGE,"E31"),sQuery(id+"F0.wireOp",EDGE,"E32"),sQuery(id+"F0.wireOp",EDGE,"E33"),sQuery(id+"F0.wireOp",EDGE,"E34"),sQuery(id+"F0.wireOp",EDGE,"E35"),sQuery(id+"F0.wireOp",EDGE,"E36"),sQuery(id+"F0.wireOp",EDGE,"E37"),sQuery(id+"F0.wireOp",EDGE,"E38"),sQuery(id+"F0.wireOp",EDGE,"E39"),sQuery(id+"F0.wireOp",EDGE,"E40"),sQuery(id+"F0.wireOp",EDGE,"E41"),sQuery(id+"F0.wireOp",EDGE,"E42"),sQuery(id+"F0.wireOp",EDGE,"E43"),sQuery(id+"F0.wireOp",EDGE,"E44"),sQuery(id+"F0.wireOp",EDGE,"E45"),sQuery(id+"F0.wireOp",EDGE,"E46"),sQuery(id+"F0.wireOp",EDGE,"E47"),sQuery(id+"F0.wireOp",EDGE,"E48"),sQuery(id+"F0.wireOp",EDGE,"E49"),sQuery(id+"F0.wireOp",EDGE,"E50"),sQuery(id+"F0.wireOp",EDGE,"E51"),sQuery(id+"F0.wireOp",EDGE,"E52"),sQuery(id+"F0.wireOp",EDGE,"E53"),sQuery(id+"F0.wireOp",EDGE,"E54"),sQuery(id+"F0.wireOp",EDGE,"E55"),sQuery(id+"F0.wireOp",EDGE,"E56"),sQuery(id+"F0.wireOp",EDGE,"E57"),sQuery(id+"F0.wireOp",EDGE,"E58"),sQuery(id+"F0.wireOp",EDGE,"E59"),sQuery(id+"F0.wireOp",EDGE,"E60"),sQuery(id+"F0.wireOp",EDGE,"E61"),sQuery(id+"F0.wireOp",EDGE,"E62"),sQuery(id+"F0.wireOp",EDGE,"E63"),sQuery(id+"F0.wireOp",EDGE,"E64"),sQuery(id+"F0.wireOp",EDGE,"E65"),sQuery(id+"F0.wireOp",EDGE,"E66"),sQuery(id+"F0.wireOp",EDGE,"E67"),sQuery(id+"F0.wireOp",EDGE,"E68"),sQuery(id+"F0.wireOp",EDGE,"E69"),sQuery(id+"F0.wireOp",EDGE,"E70"),sQuery(id+"F0.wireOp",EDGE,"E71"),sQuery(id+"F0.wireOp",EDGE,"E72"),sQuery(id+"F0.wireOp",EDGE,"E73"),sQuery(id+"F0.wireOp",EDGE,"E74"),sQuery(id+"F0.wireOp",EDGE,"E75"),sQuery(id+"F0.wireOp",EDGE,"E76"),sQuery(id+"F0.wireOp",EDGE,"E77"),sQuery(id+"F0.wireOp",EDGE,"E78"),sQuery(id+"F0.wireOp",EDGE,"E79"),sQuery(id+"F0.wireOp",EDGE,"E80"),sQuery(id+"F0.wireOp",EDGE,"E81"),sQuery(id+"F0.wireOp",EDGE,"E82"),sQuery(id+"F0.wireOp",EDGE,"E83"),sQuery(id+"F0.wireOp",EDGE,"E84"),sQuery(id+"F0.wireOp",EDGE,"E85"),sQuery(id+"F0.wireOp",EDGE,"E86"),sQuery(id+"F0.wireOp",EDGE,"E87"),sQuery(id+"F0.wireOp",EDGE,"E88"),sQuery(id+"F0.wireOp",EDGE,"E89"),sQuery(id+"F0.wireOp",EDGE,"E90"),sQuery(id+"F0.wireOp",EDGE,"E91"),sQuery(id+"F0.wireOp",EDGE,"E92"),sQuery(id+"F0.wireOp",EDGE,"E93"),sQuery(id+"F0.wireOp",EDGE,"E94"),sQuery(id+"F0.wireOp",EDGE,"E95"),sQuery(id+"F0.wireOp",EDGE,"E96"),sQuery(id+"F0.wireOp",EDGE,"E97"),sQuery(id+"F0.wireOp",EDGE,"E98"),sQuery(id+"F0.wireOp",EDGE,"E99"),sQuery(id+"F0.wireOp",EDGE,"E100"),sQuery(id+"F0.wireOp",EDGE,"E101"),sQuery(id+"F0.wireOp",EDGE,"E102"),sQuery(id+"F0.wireOp",EDGE,"E103"),sQuery(id+"F0.wireOp",EDGE,"E104"),sQuery(id+"F0.wireOp",EDGE,"E105"),sQuery(id+"F0.wireOp",EDGE,"E106"),sQuery(id+"F0.wireOp",EDGE,"E107"),sQuery(id+"F0.wireOp",EDGE,"E108"),sQuery(id+"F0.wireOp",EDGE,"E109"),sQuery(id+"F0.wireOp",EDGE,"E110"),sQuery(id+"F0.wireOp",EDGE,"E111"),sQuery(id+"F0.wireOp",EDGE,"E112"),sQuery(id+"F0.wireOp",EDGE,"E113"),sQuery(id+"F0.wireOp",EDGE,"E114"),sQuery(id+"F0.wireOp",EDGE,"E115"),sQuery(id+"F0.wireOp",EDGE,"E116"),sQuery(id+"F0.wireOp",EDGE,"E117"),sQuery(id+"F0.wireOp",EDGE,"E118"),sQuery(id+"F0.wireOp",EDGE,"E119"),sQuery(id+"F0.wireOp",EDGE,"E120"),sQuery(id+"F0.wireOp",EDGE,"E121"),sQuery(id+"F0.wireOp",EDGE,"E122"),sQuery(id+"F0.wireOp",EDGE,"E123"),sQuery(id+"F0.wireOp",EDGE,"E124"),sQuery(id+"F0.wireOp",EDGE,"E125"),sQuery(id+"F0.wireOp",EDGE,"E126")])],"isStart":true});
            var sketch = newSketch(context, id + "F7", { "sketchPlane" : qUnion([Q0])});
            skLineSegment(sketch, "E133", {"start": v(4.3, 20.63) * mm, "end": v(41.79, 20.63) * mm});
            skSolve(sketch);
        }
        {
            var Q0;
            {var subQ5=makeQuery(id+"F1.opExtrude","CAP_EDGE",EDGE,{"disambiguationData":[OSD([sQuery(id+"F0.wireOp",EDGE,"E110")])],"isStart":true});Q0=makeQuery(id+"F7.imprint","IMPRINT",FACE,{"disambiguationData":[TD([[makeQuery(id+"F7.imprint","IMPRINT",EDGE,{"derivedFrom":subQ5}),1.0]])]});}
            extrude(context, id + "F8", {"entities" : qUnion([Q0]), "operationType" : NewBodyOperationType.ADD, "oppositeDirection" : true, "depth" : 3.56 * mm});
        }
        {
            var Q0;
            Q0=makeQuery(id+"F8.opExtrude","CAP_FACE",FACE,{"disambiguationData":[OSD([sQuery(id+"F0.wireOp",EDGE,"E109"),sQuery(id+"F0.wireOp",EDGE,"E110"),sQuery(id+"F0.wireOp",EDGE,"E111"),sQuery(id+"F0.wireOp",EDGE,"E112"),sQuery(id+"F0.wireOp",EDGE,"E113"),sQuery(id+"F0.wireOp",EDGE,"E114"),sQuery(id+"F0.wireOp",EDGE,"E115"),sQuery(id+"F0.wireOp",EDGE,"E116"),sQuery(id+"F0.wireOp",EDGE,"E117"),sQuery(id+"F0.wireOp",EDGE,"E118"),sQuery(id+"F0.wireOp",EDGE,"E119"),sQuery(id+"F0.wireOp",EDGE,"E120"),sQuery(id+"F0.wireOp",EDGE,"E121"),sQuery(id+"F0.wireOp",EDGE,"E122"),sQuery(id+"F7.wireOp",EDGE,"E133")])],"isStart":false});
            var sketch = newSketch(context, id + "F9", { "sketchPlane" : qUnion([Q0])});
            skLineSegment(sketch, "E134.bottom", {"start": v(20.04, -33.33) * mm, "end": v(31.65, -33.33) * mm});
            skLineSegment(sketch, "E134.top", {"start": v(20.04, -17.27) * mm, "end": v(31.65, -17.27) * mm});
            skLineSegment(sketch, "E134.left", {"start": v(20.04, -33.33) * mm, "end": v(20.04, -17.27) * mm});
            skLineSegment(sketch, "E134.right", {"start": v(31.65, -33.33) * mm, "end": v(31.65, -17.27) * mm});
            skLineSegment(sketch, "E135", {"start": v(25.84, -17.27) * mm, "end": v(25.84, -33.33) * mm, "construction": true});
            skSolve(sketch);
        }
        {
            var Q0;
            Q0 = qSketchRegion(id + "F9", true);
            extrude(context, id + "F10", {"entities" : qUnion([Q0]), "operationType" : NewBodyOperationType.ADD, "depth" : 3.56 * mm});
        }
        {
            var Q0;
            {var subQ0=sQuery(id+"F0.wireOp",EDGE,"E122");var subQ1=sQuery(id+"F0.wireOp",EDGE,"E121");var subQ2=sQuery(id+"F0.wireOp",EDGE,"E120");var subQ3=sQuery(id+"F0.wireOp",EDGE,"E119");var subQ4=sQuery(id+"F0.wireOp",EDGE,"E118");var subQ5=sQuery(id+"F0.wireOp",EDGE,"E117");var subQ6=sQuery(id+"F0.wireOp",EDGE,"E116");var subQ7=sQuery(id+"F0.wireOp",EDGE,"E115");var subQ8=sQuery(id+"F0.wireOp",EDGE,"E114");var subQ9=sQuery(id+"F0.wireOp",EDGE,"E113");var subQ10=sQuery(id+"F0.wireOp",EDGE,"E112");var subQ11=sQuery(id+"F0.wireOp",EDGE,"E111");var subQ12=sQuery(id+"F0.wireOp",EDGE,"E110");var subQ13=sQuery(id+"F0.wireOp",EDGE,"E109");Q0=makeQuery(id+"F8.boolean.opBoolean","MERGE",FACE,{"derivedFrom":[makeQuery(id+"F1.opExtrude","CAP_FACE",FACE,{"disambiguationData":[OSD([sQuery(id+"F0.wireOp",EDGE,"E0"),sQuery(id+"F0.wireOp",EDGE,"E1"),sQuery(id+"F0.wireOp",EDGE,"E2"),sQuery(id+"F0.wireOp",EDGE,"E3"),sQuery(id+"F0.wireOp",EDGE,"E4"),sQuery(id+"F0.wireOp",EDGE,"E5"),sQuery(id+"F0.wireOp",EDGE,"E6"),sQuery(id+"F0.wireOp",EDGE,"E7"),sQuery(id+"F0.wireOp",EDGE,"E8"),sQuery(id+"F0.wireOp",EDGE,"E9"),sQuery(id+"F0.wireOp",EDGE,"E10"),sQuery(id+"F0.wireOp",EDGE,"E11"),sQuery(id+"F0.wireOp",EDGE,"E12"),sQuery(id+"F0.wireOp",EDGE,"E13"),sQuery(id+"F0.wireOp",EDGE,"E14"),sQuery(id+"F0.wireOp",EDGE,"E15"),sQuery(id+"F0.wireOp",EDGE,"E16"),sQuery(id+"F0.wireOp",EDGE,"E17"),sQuery(id+"F0.wireOp",EDGE,"E18"),sQuery(id+"F0.wireOp",EDGE,"E19"),sQuery(id+"F0.wireOp",EDGE,"E20"),sQuery(id+"F0.wireOp",EDGE,"E21"),sQuery(id+"F0.wireOp",EDGE,"E22"),sQuery(id+"F0.wireOp",EDGE,"E23"),sQuery(id+"F0.wireOp",EDGE,"E24"),sQuery(id+"F0.wireOp",EDGE,"E25"),sQuery(id+"F0.wireOp",EDGE,"E26"),sQuery(id+"F0.wireOp",EDGE,"E27"),sQuery(id+"F0.wireOp",EDGE,"E28"),sQuery(id+"F0.wireOp",EDGE,"E29"),sQuery(id+"F0.wireOp",EDGE,"E30"),sQuery(id+"F0.wireOp",EDGE,"E31"),sQuery(id+"F0.wireOp",EDGE,"E32"),sQuery(id+"F0.wireOp",EDGE,"E33"),sQuery(id+"F0.wireOp",EDGE,"E34"),sQuery(id+"F0.wireOp",EDGE,"E35"),sQuery(id+"F0.wireOp",EDGE,"E36"),sQuery(id+"F0.wireOp",EDGE,"E37"),sQuery(id+"F0.wireOp",EDGE,"E38"),sQuery(id+"F0.wireOp",EDGE,"E39"),sQuery(id+"F0.wireOp",EDGE,"E40"),sQuery(id+"F0.wireOp",EDGE,"E41"),sQuery(id+"F0.wireOp",EDGE,"E42"),sQuery(id+"F0.wireOp",EDGE,"E43"),sQuery(id+"F0.wireOp",EDGE,"E44"),sQuery(id+"F0.wireOp",EDGE,"E45"),sQuery(id+"F0.wireOp",EDGE,"E46"),sQuery(id+"F0.wireOp",EDGE,"E47"),sQuery(id+"F0.wireOp",EDGE,"E48"),sQuery(id+"F0.wireOp",EDGE,"E49"),sQuery(id+"F0.wireOp",EDGE,"E50"),sQuery(id+"F0.wireOp",EDGE,"E51"),sQuery(id+"F0.wireOp",EDGE,"E52"),sQuery(id+"F0.wireOp",EDGE,"E53"),sQuery(id+"F0.wireOp",EDGE,"E54"),sQuery(id+"F0.wireOp",EDGE,"E55"),sQuery(id+"F0.wireOp",EDGE,"E56"),sQuery(id+"F0.wireOp",EDGE,"E57"),sQuery(id+"F0.wireOp",EDGE,"E58"),sQuery(id+"F0.wireOp",EDGE,"E59"),sQuery(id+"F0.wireOp",EDGE,"E60"),sQuery(id+"F0.wireOp",EDGE,"E61"),sQuery(id+"F0.wireOp",EDGE,"E62"),sQuery(id+"F0.wireOp",EDGE,"E63"),sQuery(id+"F0.wireOp",EDGE,"E64"),sQuery(id+"F0.wireOp",EDGE,"E65"),sQuery(id+"F0.wireOp",EDGE,"E66"),sQuery(id+"F0.wireOp",EDGE,"E67"),sQuery(id+"F0.wireOp",EDGE,"E68"),sQuery(id+"F0.wireOp",EDGE,"E69"),sQuery(id+"F0.wireOp",EDGE,"E70"),sQuery(id+"F0.wireOp",EDGE,"E71"),sQuery(id+"F0.wireOp",EDGE,"E72"),sQuery(id+"F0.wireOp",EDGE,"E73"),sQuery(id+"F0.wireOp",EDGE,"E74"),sQuery(id+"F0.wireOp",EDGE,"E75"),sQuery(id+"F0.wireOp",EDGE,"E76"),sQuery(id+"F0.wireOp",EDGE,"E77"),sQuery(id+"F0.wireOp",EDGE,"E78"),sQuery(id+"F0.wireOp",EDGE,"E79"),sQuery(id+"F0.wireOp",EDGE,"E80"),sQuery(id+"F0.wireOp",EDGE,"E81"),sQuery(id+"F0.wireOp",EDGE,"E82"),sQuery(id+"F0.wireOp",EDGE,"E83"),sQuery(id+"F0.wireOp",EDGE,"E84"),sQuery(id+"F0.wireOp",EDGE,"E85"),sQuery(id+"F0.wireOp",EDGE,"E86"),sQuery(id+"F0.wireOp",EDGE,"E87"),sQuery(id+"F0.wireOp",EDGE,"E88"),sQuery(id+"F0.wireOp",EDGE,"E89"),sQuery(id+"F0.wireOp",EDGE,"E90"),sQuery(id+"F0.wireOp",EDGE,"E91"),sQuery(id+"F0.wireOp",EDGE,"E92"),sQuery(id+"F0.wireOp",EDGE,"E93"),sQuery(id+"F0.wireOp",EDGE,"E94"),sQuery(id+"F0.wireOp",EDGE,"E95"),sQuery(id+"F0.wireOp",EDGE,"E96"),sQuery(id+"F0.wireOp",EDGE,"E97"),sQuery(id+"F0.wireOp",EDGE,"E98"),sQuery(id+"F0.wireOp",EDGE,"E99"),sQuery(id+"F0.wireOp",EDGE,"E100"),sQuery(id+"F0.wireOp",EDGE,"E101"),sQuery(id+"F0.wireOp",EDGE,"E102"),sQuery(id+"F0.wireOp",EDGE,"E103"),sQuery(id+"F0.wireOp",EDGE,"E104"),sQuery(id+"F0.wireOp",EDGE,"E105"),sQuery(id+"F0.wireOp",EDGE,"E106"),sQuery(id+"F0.wireOp",EDGE,"E107"),sQuery(id+"F0.wireOp",EDGE,"E108"),subQ13,subQ12,subQ11,subQ10,subQ9,subQ8,subQ7,subQ6,subQ5,subQ4,subQ3,subQ2,subQ1,subQ0,sQuery(id+"F0.wireOp",EDGE,"E123"),sQuery(id+"F0.wireOp",EDGE,"E124"),sQuery(id+"F0.wireOp",EDGE,"E125"),sQuery(id+"F0.wireOp",EDGE,"E126")])],"isStart":true}),makeQuery(id+"F8.opExtrude","CAP_FACE",FACE,{"disambiguationData":[OSD([subQ13,subQ12,subQ11,subQ10,subQ9,subQ8,subQ7,subQ6,subQ5,subQ4,subQ3,subQ2,subQ1,subQ0,sQuery(id+"F7.wireOp",EDGE,"E133")])],"isStart":true})]});}
            var sketch = newSketch(context, id + "F11", { "sketchPlane" : qUnion([Q0])});
            skLineSegment(sketch, "E136.bottom", {"start": v(9.31, 61.28) * mm, "end": v(41.38, 61.28) * mm});
            skLineSegment(sketch, "E136.top", {"start": v(9.31, 66.14) * mm, "end": v(41.38, 66.14) * mm});
            skLineSegment(sketch, "E136.left", {"start": v(9.31, 61.28) * mm, "end": v(9.31, 66.14) * mm});
            skLineSegment(sketch, "E136.right", {"start": v(41.38, 61.28) * mm, "end": v(41.38, 66.14) * mm});
            skLineSegment(sketch, "E137.bottom", {"start": v(108.05, 61.16) * mm, "end": v(133.42, 61.16) * mm});
            skLineSegment(sketch, "E137.top", {"start": v(108.05, 72.36) * mm, "end": v(133.42, 72.36) * mm});
            skLineSegment(sketch, "E137.left", {"start": v(108.05, 61.16) * mm, "end": v(108.05, 72.36) * mm});
            skLineSegment(sketch, "E137.right", {"start": v(133.42, 61.16) * mm, "end": v(133.42, 72.36) * mm});
            skLineSegment(sketch, "E138", {"start": v(5.43, 51.48) * mm, "end": v(-1.66, 28.28) * mm});
            skLineSegment(sketch, "E139", {"start": v(-1.66, 28.28) * mm, "end": v(-10.07, 37.62) * mm});
            skLineSegment(sketch, "E140", {"start": v(-10.07, 37.62) * mm, "end": v(1.62, 52.12) * mm});
            skLineSegment(sketch, "E141", {"start": v(1.62, 52.12) * mm, "end": v(5.43, 51.48) * mm});
            skLineSegment(sketch, "E142.bottom", {"start": v(80.46, 25.02) * mm, "end": v(66.83, 25.02) * mm});
            skLineSegment(sketch, "E142.top", {"start": v(80.46, 28.5) * mm, "end": v(66.83, 28.5) * mm});
            skLineSegment(sketch, "E142.left", {"start": v(80.46, 25.02) * mm, "end": v(80.46, 28.5) * mm});
            skLineSegment(sketch, "E142.right", {"start": v(66.83, 25.02) * mm, "end": v(66.83, 28.5) * mm});
            skLineSegment(sketch, "E143", {"start": v(54.25, 29.71) * mm, "end": v(97.5, 29.6) * mm});
            skLineSegment(sketch, "E144", {"start": v(97.5, 29.6) * mm, "end": v(105.57, 52.08) * mm});
            skLineSegment(sketch, "E145", {"start": v(105.57, 52.08) * mm, "end": v(46.12, 52.08) * mm});
            skLineSegment(sketch, "E146", {"start": v(46.12, 52.08) * mm, "end": v(54.25, 29.71) * mm});
            skLineSegment(sketch, "E147.bottom", {"start": v(134.26, 53.89) * mm, "end": v(133, 53.89) * mm});
            skLineSegment(sketch, "E147.top", {"start": v(134.26, 47.34) * mm, "end": v(133, 47.34) * mm});
            skLineSegment(sketch, "E147.left", {"start": v(134.26, 53.89) * mm, "end": v(134.26, 47.34) * mm});
            skLineSegment(sketch, "E147.right", {"start": v(133, 53.89) * mm, "end": v(133, 47.34) * mm});
            skLineSegment(sketch, "E148.bottom", {"start": v(106.47, 2.03) * mm, "end": v(95.07, 2.03) * mm});
            skLineSegment(sketch, "E148.top", {"start": v(106.47, 4.25) * mm, "end": v(95.07, 4.25) * mm});
            skLineSegment(sketch, "E148.left", {"start": v(106.47, 2.03) * mm, "end": v(106.47, 4.25) * mm});
            skLineSegment(sketch, "E148.right", {"start": v(95.07, 2.03) * mm, "end": v(95.07, 4.25) * mm});
            skLineSegment(sketch, "E149.bottom", {"start": v(52.93, 4.25) * mm, "end": v(44.68, 4.25) * mm});
            skLineSegment(sketch, "E149.top", {"start": v(52.93, 2.03) * mm, "end": v(44.68, 2.03) * mm});
            skLineSegment(sketch, "E149.left", {"start": v(52.93, 4.25) * mm, "end": v(52.93, 2.03) * mm});
            skLineSegment(sketch, "E149.right", {"start": v(44.68, 4.25) * mm, "end": v(44.68, 2.03) * mm});
            skLineSegment(sketch, "E150.bottom", {"start": v(0, 0) * mm, "end": v(8.5, 0) * mm});
            skLineSegment(sketch, "E150.top", {"start": v(0, 2.24) * mm, "end": v(8.5, 2.24) * mm});
            skLineSegment(sketch, "E150.left", {"start": v(0, 0) * mm, "end": v(0, 2.24) * mm});
            skLineSegment(sketch, "E150.right", {"start": v(8.5, 0) * mm, "end": v(8.5, 2.24) * mm});
            skLineSegment(sketch, "E151", {"start": v(108.85, 23.13) * mm, "end": v(108.85, 13.22) * mm});
            skLineSegment(sketch, "E152", {"start": v(108.85, 13.22) * mm, "end": v(112.92, 10.07) * mm});
            skLineSegment(sketch, "E153", {"start": v(112.92, 10.07) * mm, "end": v(114, 25.99) * mm});
            skLineSegment(sketch, "E154", {"start": v(114, 25.99) * mm, "end": v(108.85, 23.13) * mm});
            skLineSegment(sketch, "E155", {"start": v(-3.01, 18.02) * mm, "end": v(-3.01, 23.84) * mm});
            skLineSegment(sketch, "E156", {"start": v(-3.01, 23.84) * mm, "end": v(-9.3, 26.77) * mm});
            skLineSegment(sketch, "E157", {"start": v(-9.3, 26.77) * mm, "end": v(-7.64, 16.15) * mm});
            skLineSegment(sketch, "E158", {"start": v(-7.64, 16.15) * mm, "end": v(-3.01, 18.02) * mm});
            skSolve(sketch);
        }
        {
            var Q0;
            Q0 = qSketchRegion(id + "F11", true);
            extrude(context, id + "F12", {"entities" : qUnion([Q0]), "operationType" : NewBodyOperationType.REMOVE, "oppositeDirection" : true, "depth" : 3.56 * mm});
        }
        {
            var Q0;
            {var subQ0=sQuery(id+"F9.wireOp",EDGE,"E134.left");var subQ1=sQuery(id+"F9.wireOp",EDGE,"E134.right");var subQ2=sQuery(id+"F7.wireOp",EDGE,"E133");var subQ3=sQuery(id+"F0.wireOp",EDGE,"E109");var subQ4=makeQuery(id+"F8.opExtrude","CAP_FACE",FACE,{"disambiguationData":[OSD([subQ3,sQuery(id+"F0.wireOp",EDGE,"E110"),sQuery(id+"F0.wireOp",EDGE,"E111"),sQuery(id+"F0.wireOp",EDGE,"E112"),sQuery(id+"F0.wireOp",EDGE,"E113"),sQuery(id+"F0.wireOp",EDGE,"E114"),sQuery(id+"F0.wireOp",EDGE,"E115"),sQuery(id+"F0.wireOp",EDGE,"E116"),sQuery(id+"F0.wireOp",EDGE,"E117"),sQuery(id+"F0.wireOp",EDGE,"E118"),sQuery(id+"F0.wireOp",EDGE,"E119"),sQuery(id+"F0.wireOp",EDGE,"E120"),sQuery(id+"F0.wireOp",EDGE,"E121"),sQuery(id+"F0.wireOp",EDGE,"E122"),subQ2])],"isStart":false});var subQ5=makeQuery(id+"F8.opExtrude","SWEPT_FACE",FACE,{"disambiguationData":[OSD([subQ2])]});Q0=makeQuery(id+"F10.boolean.opBoolean","SPLIT",EDGE,{"disambiguationData":[TD([subQ5,subQ4,makeQuery(id+"F10.opExtrude","CAP_FACE",FACE,{"disambiguationData":[OSD([sQuery(id+"F9.wireOp",EDGE,"E134.bottom"),sQuery(id+"F9.wireOp",EDGE,"E134.top"),subQ0,subQ1])],"isStart":true}),makeQuery(id+"F10.opExtrude","SWEPT_FACE",FACE,{"disambiguationData":[OSD([subQ0])]}),makeQuery(id+"F10.opExtrude","SWEPT_FACE",FACE,{"disambiguationData":[OSD([subQ1])]})])],"derivedFrom":makeQuery(id+"F8.boolean.opBoolean","SPLIT",EDGE,{"disambiguationData":[TD([makeQuery(id+"F1.opExtrude","SWEPT_FACE",FACE,{"disambiguationData":[OSD([subQ3])]})])],"derivedFrom":makeQuery(id+"F8.opExtrude","CAP_EDGE",EDGE,{"disambiguationData":[OSD([subQ2])],"isStart":false})})});}
            fillet(context, id + "F13", {"entities" : qUnion([Q0]), "radius" : 1.27 * mm, "tangentPropagation" : true, "allowEdgeOverflow" : false});
        }
        {
            var Q0;
            {var subQ0=sQuery(id+"F9.wireOp",EDGE,"E134.left");var subQ1=sQuery(id+"F9.wireOp",EDGE,"E134.bottom");Q0=makeQuery(id+"F10.boolean.opBoolean","SPLIT",EDGE,{"disambiguationData":[TD([makeQuery(id+"F10.opExtrude","SWEPT_FACE",FACE,{"disambiguationData":[OSD([subQ1])]})])],"derivedFrom":makeQuery(id+"F10.opExtrude","CAP_EDGE",EDGE,{"disambiguationData":[OSD([subQ0])],"isStart":true})});}
            var Q1;
            Q1=makeQuery(id+"F10.opExtrude","CAP_EDGE",EDGE,{"disambiguationData":[OSD([sQuery(id+"F9.wireOp",EDGE,"E134.bottom")])],"isStart":true});
            var Q2;
            {var subQ0=sQuery(id+"F9.wireOp",EDGE,"E134.right");var subQ1=sQuery(id+"F9.wireOp",EDGE,"E134.bottom");Q2=makeQuery(id+"F10.boolean.opBoolean","SPLIT",EDGE,{"disambiguationData":[TD([makeQuery(id+"F10.opExtrude","SWEPT_FACE",FACE,{"disambiguationData":[OSD([subQ1])]})])],"derivedFrom":makeQuery(id+"F10.opExtrude","CAP_EDGE",EDGE,{"disambiguationData":[OSD([subQ0])],"isStart":true})});}
            fillet(context, id + "F14", {"entities" : qUnion([Q0, Q1, Q2]), "radius" : 0.25 * mm, "tangentPropagation" : true, "allowEdgeOverflow" : false});
        }
        {
            var Q0;
            {var subQ0=sQuery(id+"F0.wireOp",EDGE,"E122");var subQ1=sQuery(id+"F0.wireOp",EDGE,"E121");var subQ2=sQuery(id+"F0.wireOp",EDGE,"E120");var subQ3=sQuery(id+"F0.wireOp",EDGE,"E119");var subQ4=sQuery(id+"F0.wireOp",EDGE,"E118");var subQ5=sQuery(id+"F0.wireOp",EDGE,"E117");var subQ6=sQuery(id+"F0.wireOp",EDGE,"E116");var subQ7=sQuery(id+"F0.wireOp",EDGE,"E115");var subQ8=sQuery(id+"F0.wireOp",EDGE,"E114");var subQ9=sQuery(id+"F0.wireOp",EDGE,"E113");var subQ10=sQuery(id+"F0.wireOp",EDGE,"E112");var subQ11=sQuery(id+"F0.wireOp",EDGE,"E111");var subQ12=sQuery(id+"F0.wireOp",EDGE,"E110");var subQ13=sQuery(id+"F0.wireOp",EDGE,"E109");Q0=makeQuery(id+"F8.boolean.opBoolean","MERGE",FACE,{"derivedFrom":[makeQuery(id+"F1.opExtrude","CAP_FACE",FACE,{"disambiguationData":[OSD([sQuery(id+"F0.wireOp",EDGE,"E0"),sQuery(id+"F0.wireOp",EDGE,"E1"),sQuery(id+"F0.wireOp",EDGE,"E2"),sQuery(id+"F0.wireOp",EDGE,"E3"),sQuery(id+"F0.wireOp",EDGE,"E4"),sQuery(id+"F0.wireOp",EDGE,"E5"),sQuery(id+"F0.wireOp",EDGE,"E6"),sQuery(id+"F0.wireOp",EDGE,"E7"),sQuery(id+"F0.wireOp",EDGE,"E8"),sQuery(id+"F0.wireOp",EDGE,"E9"),sQuery(id+"F0.wireOp",EDGE,"E10"),sQuery(id+"F0.wireOp",EDGE,"E11"),sQuery(id+"F0.wireOp",EDGE,"E12"),sQuery(id+"F0.wireOp",EDGE,"E13"),sQuery(id+"F0.wireOp",EDGE,"E14"),sQuery(id+"F0.wireOp",EDGE,"E15"),sQuery(id+"F0.wireOp",EDGE,"E16"),sQuery(id+"F0.wireOp",EDGE,"E17"),sQuery(id+"F0.wireOp",EDGE,"E18"),sQuery(id+"F0.wireOp",EDGE,"E19"),sQuery(id+"F0.wireOp",EDGE,"E20"),sQuery(id+"F0.wireOp",EDGE,"E21"),sQuery(id+"F0.wireOp",EDGE,"E22"),sQuery(id+"F0.wireOp",EDGE,"E23"),sQuery(id+"F0.wireOp",EDGE,"E24"),sQuery(id+"F0.wireOp",EDGE,"E25"),sQuery(id+"F0.wireOp",EDGE,"E26"),sQuery(id+"F0.wireOp",EDGE,"E27"),sQuery(id+"F0.wireOp",EDGE,"E28"),sQuery(id+"F0.wireOp",EDGE,"E29"),sQuery(id+"F0.wireOp",EDGE,"E30"),sQuery(id+"F0.wireOp",EDGE,"E31"),sQuery(id+"F0.wireOp",EDGE,"E32"),sQuery(id+"F0.wireOp",EDGE,"E33"),sQuery(id+"F0.wireOp",EDGE,"E34"),sQuery(id+"F0.wireOp",EDGE,"E35"),sQuery(id+"F0.wireOp",EDGE,"E36"),sQuery(id+"F0.wireOp",EDGE,"E37"),sQuery(id+"F0.wireOp",EDGE,"E38"),sQuery(id+"F0.wireOp",EDGE,"E39"),sQuery(id+"F0.wireOp",EDGE,"E40"),sQuery(id+"F0.wireOp",EDGE,"E41"),sQuery(id+"F0.wireOp",EDGE,"E42"),sQuery(id+"F0.wireOp",EDGE,"E43"),sQuery(id+"F0.wireOp",EDGE,"E44"),sQuery(id+"F0.wireOp",EDGE,"E45"),sQuery(id+"F0.wireOp",EDGE,"E46"),sQuery(id+"F0.wireOp",EDGE,"E47"),sQuery(id+"F0.wireOp",EDGE,"E48"),sQuery(id+"F0.wireOp",EDGE,"E49"),sQuery(id+"F0.wireOp",EDGE,"E50"),sQuery(id+"F0.wireOp",EDGE,"E51"),sQuery(id+"F0.wireOp",EDGE,"E52"),sQuery(id+"F0.wireOp",EDGE,"E53"),sQuery(id+"F0.wireOp",EDGE,"E54"),sQuery(id+"F0.wireOp",EDGE,"E55"),sQuery(id+"F0.wireOp",EDGE,"E56"),sQuery(id+"F0.wireOp",EDGE,"E57"),sQuery(id+"F0.wireOp",EDGE,"E58"),sQuery(id+"F0.wireOp",EDGE,"E59"),sQuery(id+"F0.wireOp",EDGE,"E60"),sQuery(id+"F0.wireOp",EDGE,"E61"),sQuery(id+"F0.wireOp",EDGE,"E62"),sQuery(id+"F0.wireOp",EDGE,"E63"),sQuery(id+"F0.wireOp",EDGE,"E64"),sQuery(id+"F0.wireOp",EDGE,"E65"),sQuery(id+"F0.wireOp",EDGE,"E66"),sQuery(id+"F0.wireOp",EDGE,"E67"),sQuery(id+"F0.wireOp",EDGE,"E68"),sQuery(id+"F0.wireOp",EDGE,"E69"),sQuery(id+"F0.wireOp",EDGE,"E70"),sQuery(id+"F0.wireOp",EDGE,"E71"),sQuery(id+"F0.wireOp",EDGE,"E72"),sQuery(id+"F0.wireOp",EDGE,"E73"),sQuery(id+"F0.wireOp",EDGE,"E74"),sQuery(id+"F0.wireOp",EDGE,"E75"),sQuery(id+"F0.wireOp",EDGE,"E76"),sQuery(id+"F0.wireOp",EDGE,"E77"),sQuery(id+"F0.wireOp",EDGE,"E78"),sQuery(id+"F0.wireOp",EDGE,"E79"),sQuery(id+"F0.wireOp",EDGE,"E80"),sQuery(id+"F0.wireOp",EDGE,"E81"),sQuery(id+"F0.wireOp",EDGE,"E82"),sQuery(id+"F0.wireOp",EDGE,"E83"),sQuery(id+"F0.wireOp",EDGE,"E84"),sQuery(id+"F0.wireOp",EDGE,"E85"),sQuery(id+"F0.wireOp",EDGE,"E86"),sQuery(id+"F0.wireOp",EDGE,"E87"),sQuery(id+"F0.wireOp",EDGE,"E88"),sQuery(id+"F0.wireOp",EDGE,"E89"),sQuery(id+"F0.wireOp",EDGE,"E90"),sQuery(id+"F0.wireOp",EDGE,"E91"),sQuery(id+"F0.wireOp",EDGE,"E92"),sQuery(id+"F0.wireOp",EDGE,"E93"),sQuery(id+"F0.wireOp",EDGE,"E94"),sQuery(id+"F0.wireOp",EDGE,"E95"),sQuery(id+"F0.wireOp",EDGE,"E96"),sQuery(id+"F0.wireOp",EDGE,"E97"),sQuery(id+"F0.wireOp",EDGE,"E98"),sQuery(id+"F0.wireOp",EDGE,"E99"),sQuery(id+"F0.wireOp",EDGE,"E100"),sQuery(id+"F0.wireOp",EDGE,"E101"),sQuery(id+"F0.wireOp",EDGE,"E102"),sQuery(id+"F0.wireOp",EDGE,"E103"),sQuery(id+"F0.wireOp",EDGE,"E104"),sQuery(id+"F0.wireOp",EDGE,"E105"),sQuery(id+"F0.wireOp",EDGE,"E106"),sQuery(id+"F0.wireOp",EDGE,"E107"),sQuery(id+"F0.wireOp",EDGE,"E108"),subQ13,subQ12,subQ11,subQ10,subQ9,subQ8,subQ7,subQ6,subQ5,subQ4,subQ3,subQ2,subQ1,subQ0,sQuery(id+"F0.wireOp",EDGE,"E123"),sQuery(id+"F0.wireOp",EDGE,"E124"),sQuery(id+"F0.wireOp",EDGE,"E125"),sQuery(id+"F0.wireOp",EDGE,"E126")])],"isStart":true}),makeQuery(id+"F8.opExtrude","CAP_FACE",FACE,{"disambiguationData":[OSD([subQ13,subQ12,subQ11,subQ10,subQ9,subQ8,subQ7,subQ6,subQ5,subQ4,subQ3,subQ2,subQ1,subQ0,sQuery(id+"F7.wireOp",EDGE,"E133")])],"isStart":true})]});}
            var sketch = newSketch(context, id + "F15", { "sketchPlane" : qUnion([Q0])});
            skLineSegment(sketch, "E159.bottom", {"start": v(80.46, 13.22) * mm, "end": v(69.91, 13.22) * mm});
            skLineSegment(sketch, "E159.top", {"start": v(80.46, 10.66) * mm, "end": v(69.91, 10.66) * mm});
            skLineSegment(sketch, "E159.left", {"start": v(80.46, 13.22) * mm, "end": v(80.46, 10.66) * mm});
            skLineSegment(sketch, "E159.right", {"start": v(69.91, 13.22) * mm, "end": v(69.91, 10.66) * mm});
            skSolve(sketch);
        }
        {
            var Q0;
            Q0 = qSketchRegion(id + "F15", true);
            extrude(context, id + "F16", {"entities" : qUnion([Q0]), "operationType" : NewBodyOperationType.REMOVE, "oppositeDirection" : true, "depth" : 6.35 * mm});
        }
        {
            var Q0;
            {var subQ0=sQuery(id+"F0.wireOp",EDGE,"E122");var subQ1=sQuery(id+"F0.wireOp",EDGE,"E121");var subQ2=sQuery(id+"F0.wireOp",EDGE,"E120");var subQ3=sQuery(id+"F0.wireOp",EDGE,"E119");var subQ4=sQuery(id+"F0.wireOp",EDGE,"E118");var subQ5=sQuery(id+"F0.wireOp",EDGE,"E117");var subQ6=sQuery(id+"F0.wireOp",EDGE,"E116");var subQ7=sQuery(id+"F0.wireOp",EDGE,"E115");var subQ8=sQuery(id+"F0.wireOp",EDGE,"E114");var subQ9=sQuery(id+"F0.wireOp",EDGE,"E113");var subQ10=sQuery(id+"F0.wireOp",EDGE,"E112");var subQ11=sQuery(id+"F0.wireOp",EDGE,"E111");var subQ12=sQuery(id+"F0.wireOp",EDGE,"E110");var subQ13=sQuery(id+"F0.wireOp",EDGE,"E109");Q0=makeQuery(id+"F8.boolean.opBoolean","MERGE",FACE,{"derivedFrom":[makeQuery(id+"F1.opExtrude","CAP_FACE",FACE,{"disambiguationData":[OSD([sQuery(id+"F0.wireOp",EDGE,"E0"),sQuery(id+"F0.wireOp",EDGE,"E1"),sQuery(id+"F0.wireOp",EDGE,"E2"),sQuery(id+"F0.wireOp",EDGE,"E3"),sQuery(id+"F0.wireOp",EDGE,"E4"),sQuery(id+"F0.wireOp",EDGE,"E5"),sQuery(id+"F0.wireOp",EDGE,"E6"),sQuery(id+"F0.wireOp",EDGE,"E7"),sQuery(id+"F0.wireOp",EDGE,"E8"),sQuery(id+"F0.wireOp",EDGE,"E9"),sQuery(id+"F0.wireOp",EDGE,"E10"),sQuery(id+"F0.wireOp",EDGE,"E11"),sQuery(id+"F0.wireOp",EDGE,"E12"),sQuery(id+"F0.wireOp",EDGE,"E13"),sQuery(id+"F0.wireOp",EDGE,"E14"),sQuery(id+"F0.wireOp",EDGE,"E15"),sQuery(id+"F0.wireOp",EDGE,"E16"),sQuery(id+"F0.wireOp",EDGE,"E17"),sQuery(id+"F0.wireOp",EDGE,"E18"),sQuery(id+"F0.wireOp",EDGE,"E19"),sQuery(id+"F0.wireOp",EDGE,"E20"),sQuery(id+"F0.wireOp",EDGE,"E21"),sQuery(id+"F0.wireOp",EDGE,"E22"),sQuery(id+"F0.wireOp",EDGE,"E23"),sQuery(id+"F0.wireOp",EDGE,"E24"),sQuery(id+"F0.wireOp",EDGE,"E25"),sQuery(id+"F0.wireOp",EDGE,"E26"),sQuery(id+"F0.wireOp",EDGE,"E27"),sQuery(id+"F0.wireOp",EDGE,"E28"),sQuery(id+"F0.wireOp",EDGE,"E29"),sQuery(id+"F0.wireOp",EDGE,"E30"),sQuery(id+"F0.wireOp",EDGE,"E31"),sQuery(id+"F0.wireOp",EDGE,"E32"),sQuery(id+"F0.wireOp",EDGE,"E33"),sQuery(id+"F0.wireOp",EDGE,"E34"),sQuery(id+"F0.wireOp",EDGE,"E35"),sQuery(id+"F0.wireOp",EDGE,"E36"),sQuery(id+"F0.wireOp",EDGE,"E37"),sQuery(id+"F0.wireOp",EDGE,"E38"),sQuery(id+"F0.wireOp",EDGE,"E39"),sQuery(id+"F0.wireOp",EDGE,"E40"),sQuery(id+"F0.wireOp",EDGE,"E41"),sQuery(id+"F0.wireOp",EDGE,"E42"),sQuery(id+"F0.wireOp",EDGE,"E43"),sQuery(id+"F0.wireOp",EDGE,"E44"),sQuery(id+"F0.wireOp",EDGE,"E45"),sQuery(id+"F0.wireOp",EDGE,"E46"),sQuery(id+"F0.wireOp",EDGE,"E47"),sQuery(id+"F0.wireOp",EDGE,"E48"),sQuery(id+"F0.wireOp",EDGE,"E49"),sQuery(id+"F0.wireOp",EDGE,"E50"),sQuery(id+"F0.wireOp",EDGE,"E51"),sQuery(id+"F0.wireOp",EDGE,"E52"),sQuery(id+"F0.wireOp",EDGE,"E53"),sQuery(id+"F0.wireOp",EDGE,"E54"),sQuery(id+"F0.wireOp",EDGE,"E55"),sQuery(id+"F0.wireOp",EDGE,"E56"),sQuery(id+"F0.wireOp",EDGE,"E57"),sQuery(id+"F0.wireOp",EDGE,"E58"),sQuery(id+"F0.wireOp",EDGE,"E59"),sQuery(id+"F0.wireOp",EDGE,"E60"),sQuery(id+"F0.wireOp",EDGE,"E61"),sQuery(id+"F0.wireOp",EDGE,"E62"),sQuery(id+"F0.wireOp",EDGE,"E63"),sQuery(id+"F0.wireOp",EDGE,"E64"),sQuery(id+"F0.wireOp",EDGE,"E65"),sQuery(id+"F0.wireOp",EDGE,"E66"),sQuery(id+"F0.wireOp",EDGE,"E67"),sQuery(id+"F0.wireOp",EDGE,"E68"),sQuery(id+"F0.wireOp",EDGE,"E69"),sQuery(id+"F0.wireOp",EDGE,"E70"),sQuery(id+"F0.wireOp",EDGE,"E71"),sQuery(id+"F0.wireOp",EDGE,"E72"),sQuery(id+"F0.wireOp",EDGE,"E73"),sQuery(id+"F0.wireOp",EDGE,"E74"),sQuery(id+"F0.wireOp",EDGE,"E75"),sQuery(id+"F0.wireOp",EDGE,"E76"),sQuery(id+"F0.wireOp",EDGE,"E77"),sQuery(id+"F0.wireOp",EDGE,"E78"),sQuery(id+"F0.wireOp",EDGE,"E79"),sQuery(id+"F0.wireOp",EDGE,"E80"),sQuery(id+"F0.wireOp",EDGE,"E81"),sQuery(id+"F0.wireOp",EDGE,"E82"),sQuery(id+"F0.wireOp",EDGE,"E83"),sQuery(id+"F0.wireOp",EDGE,"E84"),sQuery(id+"F0.wireOp",EDGE,"E85"),sQuery(id+"F0.wireOp",EDGE,"E86"),sQuery(id+"F0.wireOp",EDGE,"E87"),sQuery(id+"F0.wireOp",EDGE,"E88"),sQuery(id+"F0.wireOp",EDGE,"E89"),sQuery(id+"F0.wireOp",EDGE,"E90"),sQuery(id+"F0.wireOp",EDGE,"E91"),sQuery(id+"F0.wireOp",EDGE,"E92"),sQuery(id+"F0.wireOp",EDGE,"E93"),sQuery(id+"F0.wireOp",EDGE,"E94"),sQuery(id+"F0.wireOp",EDGE,"E95"),sQuery(id+"F0.wireOp",EDGE,"E96"),sQuery(id+"F0.wireOp",EDGE,"E97"),sQuery(id+"F0.wireOp",EDGE,"E98"),sQuery(id+"F0.wireOp",EDGE,"E99"),sQuery(id+"F0.wireOp",EDGE,"E100"),sQuery(id+"F0.wireOp",EDGE,"E101"),sQuery(id+"F0.wireOp",EDGE,"E102"),sQuery(id+"F0.wireOp",EDGE,"E103"),sQuery(id+"F0.wireOp",EDGE,"E104"),sQuery(id+"F0.wireOp",EDGE,"E105"),sQuery(id+"F0.wireOp",EDGE,"E106"),sQuery(id+"F0.wireOp",EDGE,"E107"),sQuery(id+"F0.wireOp",EDGE,"E108"),subQ13,subQ12,subQ11,subQ10,subQ9,subQ8,subQ7,subQ6,subQ5,subQ4,subQ3,subQ2,subQ1,subQ0,sQuery(id+"F0.wireOp",EDGE,"E123"),sQuery(id+"F0.wireOp",EDGE,"E124"),sQuery(id+"F0.wireOp",EDGE,"E125"),sQuery(id+"F0.wireOp",EDGE,"E126")])],"isStart":true}),makeQuery(id+"F8.opExtrude","CAP_FACE",FACE,{"disambiguationData":[OSD([subQ13,subQ12,subQ11,subQ10,subQ9,subQ8,subQ7,subQ6,subQ5,subQ4,subQ3,subQ2,subQ1,subQ0,sQuery(id+"F7.wireOp",EDGE,"E133")])],"isStart":true})]});}
            var sketch = newSketch(context, id + "F17", { "sketchPlane" : qUnion([Q0])});
            skArc(sketch, "E160", {"start": v(67.55, 13.22) * mm, "mid": v(75.44, 8.12) * mm, "end": v(83.32, 13.22) * mm});
            skLineSegment(sketch, "E161", {"start": v(75.44, 13.22) * mm, "end": v(75.44, 25.28) * mm, "construction": true});
            skLineSegment(sketch, "E162", {"start": v(67.55, 13.22) * mm, "end": v(83.32, 13.22) * mm});
            skPoint(sketch, "E163", {"position": v(75.44, 19.25) * mm});
            skSolve(sketch);
        }
        {
            var Q0;
            Q0 = qSketchRegion(id + "F17", true);
            extrude(context, id + "F18", {"entities" : qUnion([Q0]), "operationType" : NewBodyOperationType.ADD, "oppositeDirection" : true, "depth" : 3.56 * mm});
        }
        {
            var Q0;
            Q0=makeQuery(id+"F12.boolean.opBoolean","COPY",EDGE,{"derivedFrom":makeQuery(id+"F12.opExtrude","CAP_EDGE",EDGE,{"disambiguationData":[OSD([sQuery(id+"F11.wireOp",EDGE,"E151")])],"isStart":false})});
            var Q1;
            Q1=makeQuery(id+"F12.boolean.opBoolean","COPY",EDGE,{"derivedFrom":makeQuery(id+"F12.opExtrude","CAP_EDGE",EDGE,{"disambiguationData":[OSD([sQuery(id+"F11.wireOp",EDGE,"E148.top")])],"isStart":false})});
            var Q2;
            Q2=makeQuery(id+"F12.boolean.opBoolean","COPY",EDGE,{"derivedFrom":makeQuery(id+"F12.opExtrude","CAP_EDGE",EDGE,{"disambiguationData":[OSD([sQuery(id+"F11.wireOp",EDGE,"E147.right")])],"isStart":false})});
            var Q3;
            Q3=makeQuery(id+"F16.boolean.opBoolean","COPY",EDGE,{"derivedFrom":makeQuery(id+"F16.opExtrude","CAP_EDGE",EDGE,{"disambiguationData":[OSD([sQuery(id+"F15.wireOp",EDGE,"E159.bottom")])],"isStart":false})});
            var Q4;
            Q4=makeQuery(id+"F18.opExtrude","CAP_EDGE",EDGE,{"disambiguationData":[OSD([sQuery(id+"F17.wireOp",EDGE,"E162")])],"isStart":false});
            var Q5;
            Q5=makeQuery(id+"F12.boolean.opBoolean","COPY",EDGE,{"derivedFrom":makeQuery(id+"F12.opExtrude","CAP_EDGE",EDGE,{"disambiguationData":[OSD([sQuery(id+"F11.wireOp",EDGE,"E149.bottom")])],"isStart":false})});
            var Q6;
            Q6=makeQuery(id+"F12.boolean.opBoolean","COPY",EDGE,{"derivedFrom":makeQuery(id+"F12.opExtrude","CAP_EDGE",EDGE,{"disambiguationData":[OSD([sQuery(id+"F11.wireOp",EDGE,"E150.top")])],"isStart":false})});
            var Q7;
            Q7=makeQuery(id+"F12.boolean.opBoolean","COPY",EDGE,{"derivedFrom":makeQuery(id+"F12.opExtrude","CAP_EDGE",EDGE,{"disambiguationData":[OSD([sQuery(id+"F11.wireOp",EDGE,"E155")])],"isStart":false})});
            var Q8;
            {var subQ1=sQuery(id+"F11.wireOp",EDGE,"E138");var subQ2=sQuery(id+"F0.wireOp",EDGE,"E10");Q8=makeQuery(id+"F12.boolean.opBoolean","COPY",EDGE,{"disambiguationData":[TD([makeQuery(id+"F1.opExtrude","SWEPT_FACE",FACE,{"disambiguationData":[OSD([subQ2])]})])],"derivedFrom":makeQuery(id+"F12.opExtrude","CAP_EDGE",EDGE,{"disambiguationData":[OSD([subQ1])],"isStart":false})});}
            var Q9;
            {var subQ0=sQuery(id+"F0.wireOp",EDGE,"E14");var subQ2=sQuery(id+"F11.wireOp",EDGE,"E138");Q9=makeQuery(id+"F12.boolean.opBoolean","COPY",EDGE,{"disambiguationData":[TD([makeQuery(id+"F1.opExtrude","SWEPT_FACE",FACE,{"disambiguationData":[OSD([subQ0])]})])],"derivedFrom":makeQuery(id+"F12.opExtrude","CAP_EDGE",EDGE,{"disambiguationData":[OSD([subQ2])],"isStart":false})});}
            var Q10;
            {var subQ3=sQuery(id+"F0.wireOp",EDGE,"E20");var subQ6=sQuery(id+"F11.wireOp",EDGE,"E136.bottom");Q10=makeQuery(id+"F12.boolean.opBoolean","COPY",EDGE,{"disambiguationData":[TD([makeQuery(id+"F1.opExtrude","SWEPT_FACE",FACE,{"disambiguationData":[OSD([subQ3])]})])],"derivedFrom":makeQuery(id+"F12.opExtrude","CAP_EDGE",EDGE,{"disambiguationData":[OSD([subQ6])],"isStart":false})});}
            var Q11;
            {var subQ3=sQuery(id+"F0.wireOp",EDGE,"E24");var subQ6=sQuery(id+"F11.wireOp",EDGE,"E136.bottom");Q11=makeQuery(id+"F12.boolean.opBoolean","COPY",EDGE,{"disambiguationData":[TD([makeQuery(id+"F1.opExtrude","SWEPT_FACE",FACE,{"disambiguationData":[OSD([subQ3])]})])],"derivedFrom":makeQuery(id+"F12.opExtrude","CAP_EDGE",EDGE,{"disambiguationData":[OSD([subQ6])],"isStart":false})});}
            var Q12;
            {var subQ0=sQuery(id+"F0.wireOp",EDGE,"E28");var subQ6=sQuery(id+"F11.wireOp",EDGE,"E136.bottom");Q12=makeQuery(id+"F12.boolean.opBoolean","COPY",EDGE,{"disambiguationData":[TD([makeQuery(id+"F1.opExtrude","SWEPT_FACE",FACE,{"disambiguationData":[OSD([subQ0])]})])],"derivedFrom":makeQuery(id+"F12.opExtrude","CAP_EDGE",EDGE,{"disambiguationData":[OSD([subQ6])],"isStart":false})});}
            var Q13;
            Q13=makeQuery(id+"F12.boolean.opBoolean","COPY",EDGE,{"derivedFrom":makeQuery(id+"F12.opExtrude","CAP_EDGE",EDGE,{"disambiguationData":[OSD([sQuery(id+"F11.wireOp",EDGE,"E142.bottom")])],"isStart":false})});
            var Q14;
            {var subQ2=sQuery(id+"F0.wireOp",EDGE,"E66");var subQ3=sQuery(id+"F11.wireOp",EDGE,"E137.bottom");Q14=makeQuery(id+"F12.boolean.opBoolean","COPY",EDGE,{"disambiguationData":[TD([makeQuery(id+"F1.opExtrude","SWEPT_FACE",FACE,{"disambiguationData":[OSD([subQ2])]})])],"derivedFrom":makeQuery(id+"F12.opExtrude","CAP_EDGE",EDGE,{"disambiguationData":[OSD([subQ3])],"isStart":false})});}
            var Q15;
            {var subQ2=sQuery(id+"F11.wireOp",EDGE,"E137.bottom");var subQ5=sQuery(id+"F0.wireOp",EDGE,"E70");Q15=makeQuery(id+"F12.boolean.opBoolean","COPY",EDGE,{"disambiguationData":[TD([makeQuery(id+"F1.opExtrude","SWEPT_FACE",FACE,{"disambiguationData":[OSD([subQ5])]})])],"derivedFrom":makeQuery(id+"F12.opExtrude","CAP_EDGE",EDGE,{"disambiguationData":[OSD([subQ2])],"isStart":false})});}
            var Q16;
            {var subQ3=sQuery(id+"F0.wireOp",EDGE,"E34");var subQ4=sQuery(id+"F11.wireOp",EDGE,"E146");Q16=makeQuery(id+"F12.boolean.opBoolean","COPY",EDGE,{"disambiguationData":[TD([makeQuery(id+"F1.opExtrude","SWEPT_FACE",FACE,{"disambiguationData":[OSD([subQ3])]})])],"derivedFrom":makeQuery(id+"F12.opExtrude","CAP_EDGE",EDGE,{"disambiguationData":[OSD([subQ4])],"isStart":false})});}
            var Q17;
            {var subQ4=sQuery(id+"F11.wireOp",EDGE,"E146");var subQ5=sQuery(id+"F0.wireOp",EDGE,"E38");Q17=makeQuery(id+"F12.boolean.opBoolean","COPY",EDGE,{"disambiguationData":[TD([makeQuery(id+"F1.opExtrude","SWEPT_FACE",FACE,{"disambiguationData":[OSD([subQ5])]})])],"derivedFrom":makeQuery(id+"F12.opExtrude","CAP_EDGE",EDGE,{"disambiguationData":[OSD([subQ4])],"isStart":false})});}
            var Q18;
            {var subQ2=sQuery(id+"F11.wireOp",EDGE,"E144");var subQ5=sQuery(id+"F0.wireOp",EDGE,"E60");Q18=makeQuery(id+"F12.boolean.opBoolean","COPY",EDGE,{"disambiguationData":[TD([makeQuery(id+"F1.opExtrude","SWEPT_FACE",FACE,{"disambiguationData":[OSD([subQ5])]})])],"derivedFrom":makeQuery(id+"F12.opExtrude","CAP_EDGE",EDGE,{"disambiguationData":[OSD([subQ2])],"isStart":false})});}
            var Q19;
            {var subQ1=sQuery(id+"F0.wireOp",EDGE,"E56");var subQ4=sQuery(id+"F11.wireOp",EDGE,"E144");Q19=makeQuery(id+"F12.boolean.opBoolean","COPY",EDGE,{"disambiguationData":[TD([makeQuery(id+"F1.opExtrude","SWEPT_FACE",FACE,{"disambiguationData":[OSD([subQ1])]})])],"derivedFrom":makeQuery(id+"F12.opExtrude","CAP_EDGE",EDGE,{"disambiguationData":[OSD([subQ4])],"isStart":false})});}
            fillet(context, id + "F19", {"entities" : qUnion([Q0, Q1, Q2, Q3, Q4, Q5, Q6, Q7, Q8, Q9, Q10, Q11, Q12, Q13, Q14, Q15, Q16, Q17, Q18, Q19]), "radius" : 0.25 * mm, "tangentPropagation" : true, "allowEdgeOverflow" : false});
        }
        {
            var Q0;
            {var subQ0=sQuery(id+"F0.wireOp",EDGE,"E30");Q0=makeQuery(id+"F4.boolean.opBoolean","MERGE",FACE,{"derivedFrom":[makeQuery(id+"F1.opExtrude","SWEPT_FACE",FACE,{"disambiguationData":[OSD([subQ0])]}),makeQuery(id+"F4.opExtrude","SWEPT_FACE",FACE,{"disambiguationData":[OSD([subQ0])]})]});}
            cPlane(context, id + "F20", {"entities" : qUnion([Q0]), "cplaneType" : CPlaneType.OFFSET, "offset" : 1.59 * mm, "oppositeDirection" : true, "width" : 152.4 * mm, "height" : 152.4 * mm});
        }
        {
            var Q0;
            Q0=qCreatedBy(id+"F20.planeOp",FACE);
            var sketch = newSketch(context, id + "F21", { "sketchPlane" : qUnion([Q0])});
            skLineSegment(sketch, "E164.bottom", {"start": v(-46.24, 12.7) * mm, "end": v(-50.68, 12.7) * mm});
            skLineSegment(sketch, "E164.top", {"start": v(-46.24, 14.22) * mm, "end": v(-50.68, 14.22) * mm});
            skLineSegment(sketch, "E164.left", {"start": v(-46.24, 12.7) * mm, "end": v(-46.24, 14.22) * mm});
            skLineSegment(sketch, "E164.right", {"start": v(-50.68, 12.7) * mm, "end": v(-50.68, 14.22) * mm});
            skLineSegment(sketch, "E165", {"start": v(-50.68, 14.22) * mm, "end": v(-50.68, 17.14) * mm});
            skLineSegment(sketch, "E166", {"start": v(-50.68, 17.14) * mm, "end": v(-46.24, 14.22) * mm});
            skSolve(sketch);
        }
        {
            var Q0;
            Q0 = qSketchRegion(id + "F21", true);
            extrude(context, id + "F22", {"entities" : qUnion([Q0]), "oppositeDirection" : true, "depth" : 4.76 * mm});
        }
        {
            var Q0;
            {var subQ0=sQuery(id+"F0.wireOp",EDGE,"E26");Q0=makeQuery(id+"F4.boolean.opBoolean","MERGE",FACE,{"derivedFrom":[makeQuery(id+"F1.opExtrude","SWEPT_FACE",FACE,{"disambiguationData":[OSD([subQ0])]}),makeQuery(id+"F4.opExtrude","SWEPT_FACE",FACE,{"disambiguationData":[OSD([subQ0])]})]});}
            cPlane(context, id + "F23", {"entities" : qUnion([Q0]), "cplaneType" : CPlaneType.OFFSET, "offset" : 0 * mm, "oppositeDirection" : true, "width" : 152.4 * mm, "height" : 152.4 * mm});
        }
        {
            var Q0;
            Q0=qCreatedBy(id+"F23.planeOp",FACE);
            var sketch = newSketch(context, id + "F24", { "sketchPlane" : qUnion([Q0])});
            skLineSegment(sketch, "E167.0.0", {"start": v(-50.68, 12.7) * mm, "end": v(-46.24, 12.7) * mm});
            skLineSegment(sketch, "E167.0.1", {"start": v(-46.24, 12.7) * mm, "end": v(-46.24, 14.22) * mm});
            skLineSegment(sketch, "E167.0.2", {"start": v(-46.24, 14.22) * mm, "end": v(-50.68, 17.14) * mm});
            skLineSegment(sketch, "E167.0.3", {"start": v(-50.68, 17.14) * mm, "end": v(-50.68, 12.7) * mm});
            skSolve(sketch);
        }
        {
            var Q0;
            Q0 = qSketchRegion(id + "F24", true);
            var Q1;
            {var subQ0=sQuery(id+"F0.wireOp",EDGE,"E24");Q1=makeQuery(id+"F4.boolean.opBoolean","MERGE",FACE,{"derivedFrom":[makeQuery(id+"F1.opExtrude","SWEPT_FACE",FACE,{"disambiguationData":[OSD([subQ0])]}),makeQuery(id+"F4.opExtrude","SWEPT_FACE",FACE,{"disambiguationData":[OSD([subQ0])]})]});}
            extrude(context, id + "F25", {"entities" : qUnion([Q0]), "operationType" : NewBodyOperationType.ADD, "endBound" : BoundingType.UP_TO_SURFACE, "oppositeDirection" : true, "endBoundEntityFace" : qUnion([Q1]), "depth" : 25.4 * mm});
        }
    });
